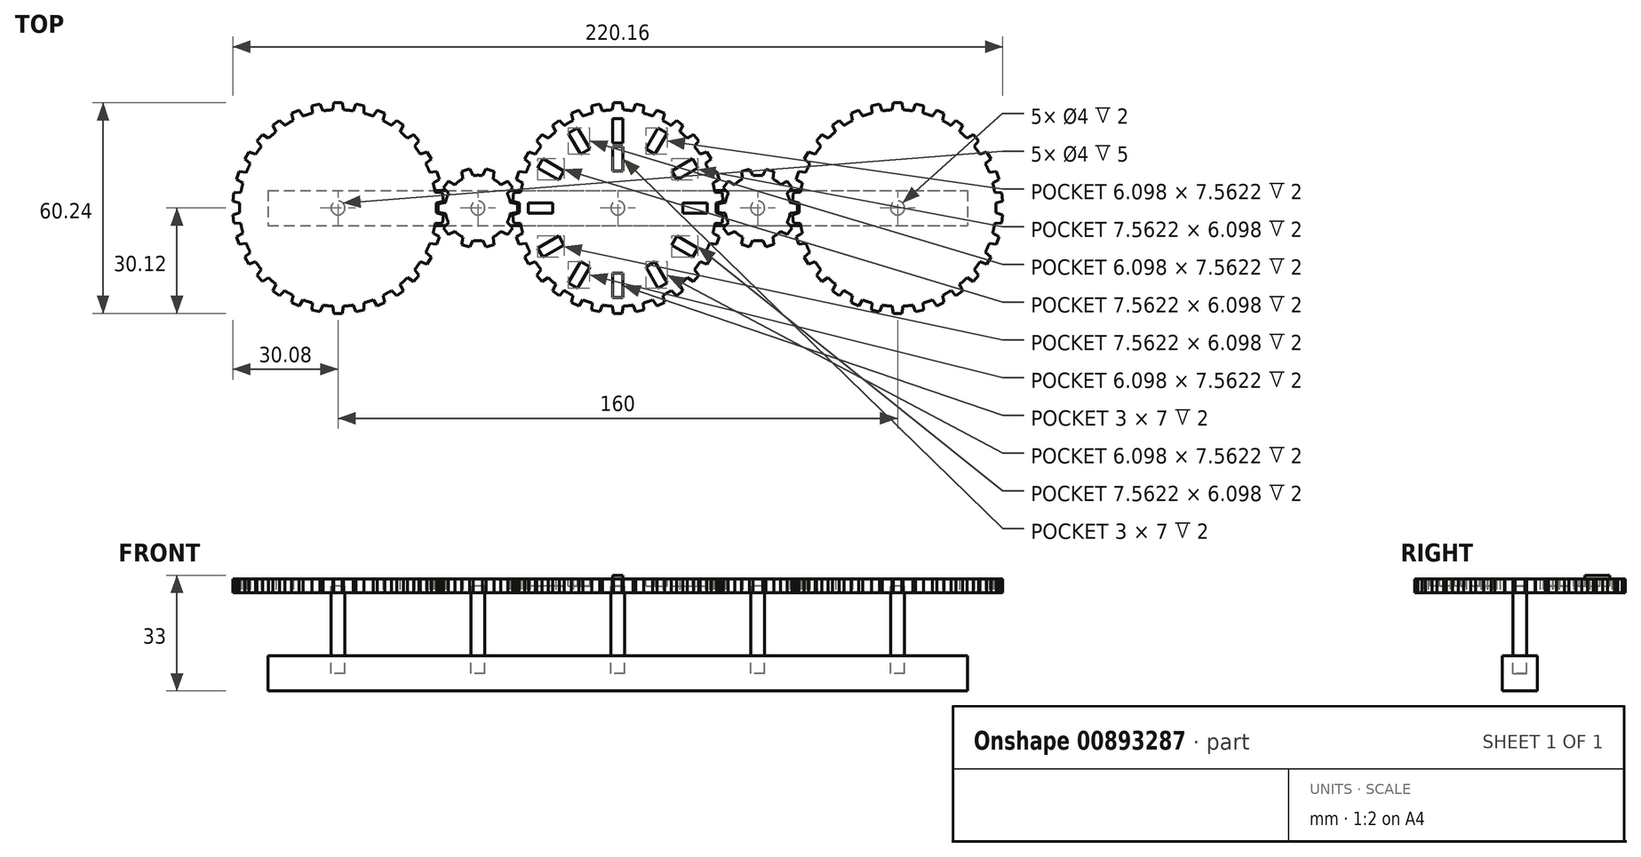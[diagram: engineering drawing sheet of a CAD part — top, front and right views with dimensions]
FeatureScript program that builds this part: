
annotation { "Feature Type Name" : "Feature", "Feature Type Description" : "" }
export const myFeature = defineFeature(function(context is Context, id is Id, definition is map)
    precondition{}
    {
        {
            var Q0;
            Q0=qCreatedBy(makeId("Top.planeOp"),FACE);
            var sketch = newSketch(context, id + "F0", { "sketchPlane" : qUnion([Q0])});
            skCircle(sketch, "E0", {"center": v(0, 0) * mm, "radius": 28.13 * mm});
            skLineSegment(sketch, "E1", {"start": v(-1.54, 28.08) * mm, "end": v(-1.18, 30.13) * mm});
            skLineSegment(sketch, "E2", {"start": v(-1.18, 30.13) * mm, "end": v(0, 30.13) * mm});
            skLineSegment(sketch, "E3.MirrorCS", {"start": v(1.54, 28.08) * mm, "end": v(1.18, 30.13) * mm});
            skLineSegment(sketch, "E4.MirrorCS", {"start": v(1.18, 30.13) * mm, "end": v(0, 30.13) * mm});
            skLineSegment(sketch, "E5.1.0", {"start": v(-7.34, 27.15) * mm, "end": v(-7.42, 29.22) * mm});
            skLineSegment(sketch, "E5.1.1", {"start": v(-7.42, 29.22) * mm, "end": v(-6.26, 29.47) * mm});
            skLineSegment(sketch, "E5.1.2", {"start": v(-5.11, 29.71) * mm, "end": v(-6.26, 29.47) * mm});
            skLineSegment(sketch, "E5.1.3", {"start": v(-4.33, 27.79) * mm, "end": v(-5.11, 29.71) * mm});
            skLineSegment(sketch, "E5.2.0", {"start": v(-12.83, 25.03) * mm, "end": v(-13.33, 27.04) * mm});
            skLineSegment(sketch, "E5.2.1", {"start": v(-13.33, 27.04) * mm, "end": v(-12.25, 27.52) * mm});
            skLineSegment(sketch, "E5.2.2", {"start": v(-11.18, 28) * mm, "end": v(-12.25, 27.52) * mm});
            skLineSegment(sketch, "E5.2.3", {"start": v(-10.02, 26.28) * mm, "end": v(-11.18, 28) * mm});
            skLineSegment(sketch, "E6.1.3.0", {"start": v(-17.75, 21.82) * mm, "end": v(-18.66, 23.68) * mm});
            skLineSegment(sketch, "E6.3.3.0", {"start": v(-18.66, 23.68) * mm, "end": v(-17.7, 24.37) * mm});
            skLineSegment(sketch, "E6.6.3.0", {"start": v(-16.75, 25.06) * mm, "end": v(-17.7, 24.37) * mm});
            skLineSegment(sketch, "E6.9.3.0", {"start": v(-15.26, 23.62) * mm, "end": v(-16.75, 25.06) * mm});
            skLineSegment(sketch, "E6.1.4.0", {"start": v(-21.9, 17.65) * mm, "end": v(-23.18, 19.28) * mm});
            skLineSegment(sketch, "E6.3.4.0", {"start": v(-23.18, 19.28) * mm, "end": v(-22.39, 20.16) * mm});
            skLineSegment(sketch, "E6.6.4.0", {"start": v(-21.6, 21.03) * mm, "end": v(-22.39, 20.16) * mm});
            skLineSegment(sketch, "E6.9.4.0", {"start": v(-19.84, 19.93) * mm, "end": v(-21.6, 21.03) * mm});
            skLineSegment(sketch, "E6.1.5.0", {"start": v(-25.09, 12.7) * mm, "end": v(-26.68, 14.04) * mm});
            skLineSegment(sketch, "E6.3.5.0", {"start": v(-26.68, 14.04) * mm, "end": v(-26.09, 15.06) * mm});
            skLineSegment(sketch, "E6.6.5.0", {"start": v(-25.5, 16.08) * mm, "end": v(-26.09, 15.06) * mm});
            skLineSegment(sketch, "E6.9.5.0", {"start": v(-23.55, 15.37) * mm, "end": v(-25.5, 16.08) * mm});
            skLineSegment(sketch, "E6.1.6.0", {"start": v(-27.18, 7.22) * mm, "end": v(-29.01, 8.19) * mm});
            skLineSegment(sketch, "E6.3.6.0", {"start": v(-29.01, 8.19) * mm, "end": v(-28.65, 9.3) * mm});
            skLineSegment(sketch, "E6.6.6.0", {"start": v(-28.29, 10.43) * mm, "end": v(-28.65, 9.3) * mm});
            skLineSegment(sketch, "E6.9.6.0", {"start": v(-26.23, 10.14) * mm, "end": v(-28.29, 10.43) * mm});
            skLineSegment(sketch, "E6.1.7.0", {"start": v(-28.09, 1.4) * mm, "end": v(-30.08, 1.98) * mm});
            skLineSegment(sketch, "E6.3.7.0", {"start": v(-30.08, 1.98) * mm, "end": v(-29.96, 3.15) * mm});
            skLineSegment(sketch, "E6.6.7.0", {"start": v(-29.84, 4.32) * mm, "end": v(-29.96, 3.15) * mm});
            skLineSegment(sketch, "E6.9.7.0", {"start": v(-27.77, 4.47) * mm, "end": v(-29.84, 4.32) * mm});
            skLineSegment(sketch, "E6.1.8.0", {"start": v(-27.77, -4.47) * mm, "end": v(-29.84, -4.32) * mm});
            skLineSegment(sketch, "E6.3.8.0", {"start": v(-29.84, -4.32) * mm, "end": v(-29.96, -3.15) * mm});
            skLineSegment(sketch, "E6.6.8.0", {"start": v(-30.08, -1.98) * mm, "end": v(-29.96, -3.15) * mm});
            skLineSegment(sketch, "E6.9.8.0", {"start": v(-28.09, -1.4) * mm, "end": v(-30.08, -1.98) * mm});
            skLineSegment(sketch, "E6.1.9.0", {"start": v(-26.23, -10.14) * mm, "end": v(-28.29, -10.43) * mm});
            skLineSegment(sketch, "E6.3.9.0", {"start": v(-28.29, -10.43) * mm, "end": v(-28.65, -9.3) * mm});
            skLineSegment(sketch, "E6.6.9.0", {"start": v(-29.01, -8.19) * mm, "end": v(-28.65, -9.3) * mm});
            skLineSegment(sketch, "E6.9.9.0", {"start": v(-27.18, -7.22) * mm, "end": v(-29.01, -8.19) * mm});
            skLineSegment(sketch, "E7.1.10.0", {"start": v(-23.55, -15.37) * mm, "end": v(-25.5, -16.08) * mm});
            skLineSegment(sketch, "E7.3.10.0", {"start": v(-25.5, -16.08) * mm, "end": v(-26.09, -15.06) * mm});
            skLineSegment(sketch, "E7.6.10.0", {"start": v(-26.68, -14.04) * mm, "end": v(-26.09, -15.06) * mm});
            skLineSegment(sketch, "E7.9.10.0", {"start": v(-25.09, -12.7) * mm, "end": v(-26.68, -14.04) * mm});
            skLineSegment(sketch, "E7.1.11.0", {"start": v(-19.84, -19.93) * mm, "end": v(-21.6, -21.03) * mm});
            skLineSegment(sketch, "E7.3.11.0", {"start": v(-21.6, -21.03) * mm, "end": v(-22.39, -20.16) * mm});
            skLineSegment(sketch, "E7.6.11.0", {"start": v(-23.18, -19.28) * mm, "end": v(-22.39, -20.16) * mm});
            skLineSegment(sketch, "E7.9.11.0", {"start": v(-21.9, -17.65) * mm, "end": v(-23.18, -19.28) * mm});
            skLineSegment(sketch, "E7.1.12.0", {"start": v(-15.26, -23.62) * mm, "end": v(-16.75, -25.06) * mm});
            skLineSegment(sketch, "E7.3.12.0", {"start": v(-16.75, -25.06) * mm, "end": v(-17.7, -24.37) * mm});
            skLineSegment(sketch, "E7.6.12.0", {"start": v(-18.66, -23.68) * mm, "end": v(-17.7, -24.37) * mm});
            skLineSegment(sketch, "E7.9.12.0", {"start": v(-17.75, -21.82) * mm, "end": v(-18.66, -23.68) * mm});
            skLineSegment(sketch, "E7.1.13.0", {"start": v(-10.02, -26.28) * mm, "end": v(-11.18, -28) * mm});
            skLineSegment(sketch, "E7.3.13.0", {"start": v(-11.18, -28) * mm, "end": v(-12.25, -27.52) * mm});
            skLineSegment(sketch, "E7.6.13.0", {"start": v(-13.33, -27.04) * mm, "end": v(-12.25, -27.52) * mm});
            skLineSegment(sketch, "E7.9.13.0", {"start": v(-12.83, -25.03) * mm, "end": v(-13.33, -27.04) * mm});
            skLineSegment(sketch, "E7.1.14.0", {"start": v(-4.33, -27.79) * mm, "end": v(-5.11, -29.71) * mm});
            skLineSegment(sketch, "E7.3.14.0", {"start": v(-5.11, -29.71) * mm, "end": v(-6.26, -29.47) * mm});
            skLineSegment(sketch, "E7.6.14.0", {"start": v(-7.42, -29.22) * mm, "end": v(-6.26, -29.47) * mm});
            skLineSegment(sketch, "E7.9.14.0", {"start": v(-7.34, -27.15) * mm, "end": v(-7.42, -29.22) * mm});
            skLineSegment(sketch, "E7.1.15.0", {"start": v(1.54, -28.08) * mm, "end": v(1.18, -30.13) * mm});
            skLineSegment(sketch, "E7.3.15.0", {"start": v(1.18, -30.13) * mm, "end": v(0, -30.13) * mm});
            skLineSegment(sketch, "E7.6.15.0", {"start": v(-1.18, -30.13) * mm, "end": v(0, -30.13) * mm});
            skLineSegment(sketch, "E7.9.15.0", {"start": v(-1.54, -28.08) * mm, "end": v(-1.18, -30.13) * mm});
            skLineSegment(sketch, "E7.1.16.0", {"start": v(7.34, -27.15) * mm, "end": v(7.42, -29.22) * mm});
            skLineSegment(sketch, "E7.3.16.0", {"start": v(7.42, -29.22) * mm, "end": v(6.26, -29.47) * mm});
            skLineSegment(sketch, "E7.6.16.0", {"start": v(5.11, -29.71) * mm, "end": v(6.26, -29.47) * mm});
            skLineSegment(sketch, "E7.9.16.0", {"start": v(4.33, -27.79) * mm, "end": v(5.11, -29.71) * mm});
            skLineSegment(sketch, "E7.1.17.0", {"start": v(12.83, -25.03) * mm, "end": v(13.33, -27.04) * mm});
            skLineSegment(sketch, "E7.3.17.0", {"start": v(13.33, -27.04) * mm, "end": v(12.25, -27.52) * mm});
            skLineSegment(sketch, "E7.6.17.0", {"start": v(11.18, -28) * mm, "end": v(12.25, -27.52) * mm});
            skLineSegment(sketch, "E7.9.17.0", {"start": v(10.02, -26.28) * mm, "end": v(11.18, -28) * mm});
            skLineSegment(sketch, "E7.1.18.0", {"start": v(17.75, -21.82) * mm, "end": v(18.66, -23.68) * mm});
            skLineSegment(sketch, "E7.3.18.0", {"start": v(18.66, -23.68) * mm, "end": v(17.7, -24.37) * mm});
            skLineSegment(sketch, "E7.6.18.0", {"start": v(16.75, -25.06) * mm, "end": v(17.7, -24.37) * mm});
            skLineSegment(sketch, "E7.9.18.0", {"start": v(15.26, -23.62) * mm, "end": v(16.75, -25.06) * mm});
            skLineSegment(sketch, "E7.1.19.0", {"start": v(21.9, -17.65) * mm, "end": v(23.18, -19.28) * mm});
            skLineSegment(sketch, "E7.3.19.0", {"start": v(23.18, -19.28) * mm, "end": v(22.39, -20.16) * mm});
            skLineSegment(sketch, "E7.6.19.0", {"start": v(21.6, -21.03) * mm, "end": v(22.39, -20.16) * mm});
            skLineSegment(sketch, "E7.9.19.0", {"start": v(19.84, -19.93) * mm, "end": v(21.6, -21.03) * mm});
            skLineSegment(sketch, "E7.1.20.0", {"start": v(25.09, -12.7) * mm, "end": v(26.68, -14.04) * mm});
            skLineSegment(sketch, "E7.3.20.0", {"start": v(26.68, -14.04) * mm, "end": v(26.09, -15.06) * mm});
            skLineSegment(sketch, "E7.6.20.0", {"start": v(25.5, -16.08) * mm, "end": v(26.09, -15.06) * mm});
            skLineSegment(sketch, "E7.9.20.0", {"start": v(23.55, -15.37) * mm, "end": v(25.5, -16.08) * mm});
            skLineSegment(sketch, "E7.1.21.0", {"start": v(27.18, -7.22) * mm, "end": v(29.01, -8.19) * mm});
            skLineSegment(sketch, "E7.3.21.0", {"start": v(29.01, -8.19) * mm, "end": v(28.65, -9.3) * mm});
            skLineSegment(sketch, "E7.6.21.0", {"start": v(28.29, -10.43) * mm, "end": v(28.65, -9.3) * mm});
            skLineSegment(sketch, "E7.9.21.0", {"start": v(26.23, -10.14) * mm, "end": v(28.29, -10.43) * mm});
            skLineSegment(sketch, "E7.1.22.0", {"start": v(28.09, -1.4) * mm, "end": v(30.08, -1.98) * mm});
            skLineSegment(sketch, "E7.3.22.0", {"start": v(30.08, -1.98) * mm, "end": v(29.96, -3.15) * mm});
            skLineSegment(sketch, "E7.6.22.0", {"start": v(29.84, -4.32) * mm, "end": v(29.96, -3.15) * mm});
            skLineSegment(sketch, "E7.9.22.0", {"start": v(27.77, -4.47) * mm, "end": v(29.84, -4.32) * mm});
            skLineSegment(sketch, "E7.1.23.0", {"start": v(27.77, 4.47) * mm, "end": v(29.84, 4.32) * mm});
            skLineSegment(sketch, "E7.3.23.0", {"start": v(29.84, 4.32) * mm, "end": v(29.96, 3.15) * mm});
            skLineSegment(sketch, "E7.6.23.0", {"start": v(30.08, 1.98) * mm, "end": v(29.96, 3.15) * mm});
            skLineSegment(sketch, "E7.9.23.0", {"start": v(28.09, 1.4) * mm, "end": v(30.08, 1.98) * mm});
            skLineSegment(sketch, "E7.1.24.0", {"start": v(26.23, 10.14) * mm, "end": v(28.29, 10.43) * mm});
            skLineSegment(sketch, "E7.3.24.0", {"start": v(28.29, 10.43) * mm, "end": v(28.65, 9.3) * mm});
            skLineSegment(sketch, "E7.6.24.0", {"start": v(29.01, 8.19) * mm, "end": v(28.65, 9.3) * mm});
            skLineSegment(sketch, "E7.9.24.0", {"start": v(27.18, 7.22) * mm, "end": v(29.01, 8.19) * mm});
            skLineSegment(sketch, "E7.1.25.0", {"start": v(23.55, 15.37) * mm, "end": v(25.5, 16.08) * mm});
            skLineSegment(sketch, "E7.3.25.0", {"start": v(25.5, 16.08) * mm, "end": v(26.09, 15.06) * mm});
            skLineSegment(sketch, "E7.6.25.0", {"start": v(26.68, 14.04) * mm, "end": v(26.09, 15.06) * mm});
            skLineSegment(sketch, "E7.9.25.0", {"start": v(25.09, 12.7) * mm, "end": v(26.68, 14.04) * mm});
            skLineSegment(sketch, "E7.1.26.0", {"start": v(19.84, 19.93) * mm, "end": v(21.6, 21.03) * mm});
            skLineSegment(sketch, "E7.3.26.0", {"start": v(21.6, 21.03) * mm, "end": v(22.39, 20.16) * mm});
            skLineSegment(sketch, "E7.6.26.0", {"start": v(23.18, 19.28) * mm, "end": v(22.39, 20.16) * mm});
            skLineSegment(sketch, "E7.9.26.0", {"start": v(21.9, 17.65) * mm, "end": v(23.18, 19.28) * mm});
            skLineSegment(sketch, "E7.1.27.0", {"start": v(15.26, 23.62) * mm, "end": v(16.75, 25.06) * mm});
            skLineSegment(sketch, "E7.3.27.0", {"start": v(16.75, 25.06) * mm, "end": v(17.7, 24.37) * mm});
            skLineSegment(sketch, "E7.6.27.0", {"start": v(18.66, 23.68) * mm, "end": v(17.7, 24.37) * mm});
            skLineSegment(sketch, "E7.9.27.0", {"start": v(17.75, 21.82) * mm, "end": v(18.66, 23.68) * mm});
            skLineSegment(sketch, "E7.1.28.0", {"start": v(10.02, 26.28) * mm, "end": v(11.18, 28) * mm});
            skLineSegment(sketch, "E7.3.28.0", {"start": v(11.18, 28) * mm, "end": v(12.25, 27.52) * mm});
            skLineSegment(sketch, "E7.6.28.0", {"start": v(13.33, 27.04) * mm, "end": v(12.25, 27.52) * mm});
            skLineSegment(sketch, "E7.9.28.0", {"start": v(12.83, 25.03) * mm, "end": v(13.33, 27.04) * mm});
            skLineSegment(sketch, "E7.1.29.0", {"start": v(4.33, 27.79) * mm, "end": v(5.11, 29.71) * mm});
            skLineSegment(sketch, "E7.3.29.0", {"start": v(5.11, 29.71) * mm, "end": v(6.26, 29.47) * mm});
            skLineSegment(sketch, "E7.6.29.0", {"start": v(7.42, 29.22) * mm, "end": v(6.26, 29.47) * mm});
            skLineSegment(sketch, "E7.9.29.0", {"start": v(7.34, 27.15) * mm, "end": v(7.42, 29.22) * mm});
            skSolve(sketch);
        }
        {
            var Q0;
            Q0 = qSketchRegion(id + "F0", true);
            extrude(context, id + "F1", {"entities" : qUnion([Q0]), "endBound" : BoundingType.SYMMETRIC, "depth" : 4 * mm, "offsetDistance" : 25 * mm});
        }
        {
            var Q0;
            Q0=qCreatedBy(makeId("Top.planeOp"),FACE);
            var sketch = newSketch(context, id + "F2", { "sketchPlane" : qUnion([Q0])});
            skCircle(sketch, "E8", {"center": v(40, 0) * mm, "radius": 9.38 * mm});
            skLineSegment(sketch, "E9", {"start": v(30.75, 1.54) * mm, "end": v(28.69, 1.18) * mm});
            skLineSegment(sketch, "E10", {"start": v(28.69, 1.18) * mm, "end": v(28.69, 0) * mm});
            skLineSegment(sketch, "E11.MirrorCS", {"start": v(28.69, -1.18) * mm, "end": v(28.69, 0) * mm});
            skLineSegment(sketch, "E12.MirrorCS", {"start": v(30.75, -1.54) * mm, "end": v(28.69, -1.18) * mm});
            skLineSegment(sketch, "E13.1.0", {"start": v(31.61, -4.19) * mm, "end": v(30.15, -5.7) * mm});
            skLineSegment(sketch, "E13.1.1", {"start": v(30.15, -5.7) * mm, "end": v(30.85, -6.65) * mm});
            skLineSegment(sketch, "E13.1.2", {"start": v(31.54, -7.6) * mm, "end": v(30.85, -6.65) * mm});
            skLineSegment(sketch, "E13.1.3", {"start": v(33.43, -6.68) * mm, "end": v(31.54, -7.6) * mm});
            skLineSegment(sketch, "E13.2.0", {"start": v(35.68, -8.32) * mm, "end": v(35.38, -10.4) * mm});
            skLineSegment(sketch, "E13.2.1", {"start": v(35.38, -10.4) * mm, "end": v(36.5, -10.76) * mm});
            skLineSegment(sketch, "E13.2.2", {"start": v(37.62, -11.12) * mm, "end": v(36.5, -10.76) * mm});
            skLineSegment(sketch, "E13.2.3", {"start": v(38.6, -9.27) * mm, "end": v(37.62, -11.12) * mm});
            skLineSegment(sketch, "E14.2.3.0", {"start": v(41.4, -9.27) * mm, "end": v(42.38, -11.12) * mm});
            skLineSegment(sketch, "E14.3.3.0", {"start": v(42.38, -11.12) * mm, "end": v(43.5, -10.76) * mm});
            skLineSegment(sketch, "E14.6.3.0", {"start": v(44.62, -10.4) * mm, "end": v(43.5, -10.76) * mm});
            skLineSegment(sketch, "E14.9.3.0", {"start": v(44.32, -8.32) * mm, "end": v(44.62, -10.4) * mm});
            skLineSegment(sketch, "E14.2.4.0", {"start": v(46.57, -6.68) * mm, "end": v(48.46, -7.6) * mm});
            skLineSegment(sketch, "E14.3.4.0", {"start": v(48.46, -7.6) * mm, "end": v(49.15, -6.65) * mm});
            skLineSegment(sketch, "E14.6.4.0", {"start": v(49.85, -5.7) * mm, "end": v(49.15, -6.65) * mm});
            skLineSegment(sketch, "E14.9.4.0", {"start": v(48.39, -4.19) * mm, "end": v(49.85, -5.7) * mm});
            skLineSegment(sketch, "E14.2.5.0", {"start": v(49.25, -1.54) * mm, "end": v(51.31, -1.18) * mm});
            skLineSegment(sketch, "E14.3.5.0", {"start": v(51.31, -1.18) * mm, "end": v(51.31, 0) * mm});
            skLineSegment(sketch, "E14.6.5.0", {"start": v(51.31, 1.18) * mm, "end": v(51.31, 0) * mm});
            skLineSegment(sketch, "E14.9.5.0", {"start": v(49.25, 1.54) * mm, "end": v(51.31, 1.18) * mm});
            skLineSegment(sketch, "E14.2.6.0", {"start": v(48.39, 4.19) * mm, "end": v(49.85, 5.7) * mm});
            skLineSegment(sketch, "E14.3.6.0", {"start": v(49.85, 5.7) * mm, "end": v(49.15, 6.65) * mm});
            skLineSegment(sketch, "E14.6.6.0", {"start": v(48.46, 7.6) * mm, "end": v(49.15, 6.65) * mm});
            skLineSegment(sketch, "E14.9.6.0", {"start": v(46.57, 6.68) * mm, "end": v(48.46, 7.6) * mm});
            skLineSegment(sketch, "E14.2.7.0", {"start": v(44.32, 8.32) * mm, "end": v(44.62, 10.4) * mm});
            skLineSegment(sketch, "E14.3.7.0", {"start": v(44.62, 10.4) * mm, "end": v(43.5, 10.76) * mm});
            skLineSegment(sketch, "E14.6.7.0", {"start": v(42.38, 11.12) * mm, "end": v(43.5, 10.76) * mm});
            skLineSegment(sketch, "E14.9.7.0", {"start": v(41.4, 9.27) * mm, "end": v(42.38, 11.12) * mm});
            skLineSegment(sketch, "E14.2.8.0", {"start": v(38.6, 9.27) * mm, "end": v(37.62, 11.12) * mm});
            skLineSegment(sketch, "E14.3.8.0", {"start": v(37.62, 11.12) * mm, "end": v(36.5, 10.76) * mm});
            skLineSegment(sketch, "E14.6.8.0", {"start": v(35.38, 10.4) * mm, "end": v(36.5, 10.76) * mm});
            skLineSegment(sketch, "E14.9.8.0", {"start": v(35.68, 8.32) * mm, "end": v(35.38, 10.4) * mm});
            skLineSegment(sketch, "E14.2.9.0", {"start": v(33.43, 6.68) * mm, "end": v(31.54, 7.6) * mm});
            skLineSegment(sketch, "E14.3.9.0", {"start": v(31.54, 7.6) * mm, "end": v(30.85, 6.65) * mm});
            skLineSegment(sketch, "E14.6.9.0", {"start": v(30.15, 5.7) * mm, "end": v(30.85, 6.65) * mm});
            skLineSegment(sketch, "E14.9.9.0", {"start": v(31.61, 4.19) * mm, "end": v(30.15, 5.7) * mm});
            skCircle(sketch, "E15.MirrorC", {"center": v(-40, 0) * mm, "radius": 9.38 * mm});
            skLineSegment(sketch, "E16", {"start": v(-30.75, 1.55) * mm, "end": v(-28.62, 1.18) * mm});
            skLineSegment(sketch, "E17", {"start": v(-28.62, 1.18) * mm, "end": v(-28.62, 0) * mm});
            skLineSegment(sketch, "E18.MirrorCS", {"start": v(-30.75, -1.55) * mm, "end": v(-28.62, -1.18) * mm});
            skLineSegment(sketch, "E19.MirrorCS", {"start": v(-28.62, -1.18) * mm, "end": v(-28.62, 0) * mm});
            skLineSegment(sketch, "E20.1.0", {"start": v(-33.43, 6.7) * mm, "end": v(-31.49, 7.64) * mm});
            skLineSegment(sketch, "E20.1.1", {"start": v(-31.49, 7.64) * mm, "end": v(-30.8, 6.69) * mm});
            skLineSegment(sketch, "E20.1.2", {"start": v(-30.1, 5.73) * mm, "end": v(-30.8, 6.69) * mm});
            skLineSegment(sketch, "E20.1.3", {"start": v(-31.6, 4.18) * mm, "end": v(-30.1, 5.73) * mm});
            skLineSegment(sketch, "E20.2.0", {"start": v(-38.62, 9.27) * mm, "end": v(-37.6, 11.18) * mm});
            skLineSegment(sketch, "E20.2.1", {"start": v(-37.6, 11.18) * mm, "end": v(-36.48, 10.82) * mm});
            skLineSegment(sketch, "E20.2.2", {"start": v(-35.36, 10.45) * mm, "end": v(-36.48, 10.82) * mm});
            skLineSegment(sketch, "E20.2.3", {"start": v(-35.67, 8.31) * mm, "end": v(-35.36, 10.45) * mm});
            skLineSegment(sketch, "E21.1.3.0", {"start": v(-44.33, 8.31) * mm, "end": v(-44.64, 10.45) * mm});
            skLineSegment(sketch, "E21.3.3.0", {"start": v(-44.64, 10.45) * mm, "end": v(-43.52, 10.82) * mm});
            skLineSegment(sketch, "E21.6.3.0", {"start": v(-42.4, 11.18) * mm, "end": v(-43.52, 10.82) * mm});
            skLineSegment(sketch, "E21.9.3.0", {"start": v(-41.38, 9.27) * mm, "end": v(-42.4, 11.18) * mm});
            skLineSegment(sketch, "E21.1.4.0", {"start": v(-48.4, 4.18) * mm, "end": v(-49.9, 5.73) * mm});
            skLineSegment(sketch, "E21.3.4.0", {"start": v(-49.9, 5.73) * mm, "end": v(-49.2, 6.69) * mm});
            skLineSegment(sketch, "E21.6.4.0", {"start": v(-48.51, 7.64) * mm, "end": v(-49.2, 6.69) * mm});
            skLineSegment(sketch, "E21.9.4.0", {"start": v(-46.57, 6.7) * mm, "end": v(-48.51, 7.64) * mm});
            skLineSegment(sketch, "E21.1.5.0", {"start": v(-49.25, -1.55) * mm, "end": v(-51.38, -1.18) * mm});
            skLineSegment(sketch, "E21.3.5.0", {"start": v(-51.38, -1.18) * mm, "end": v(-51.38, 0) * mm});
            skLineSegment(sketch, "E21.6.5.0", {"start": v(-51.38, 1.18) * mm, "end": v(-51.38, 0) * mm});
            skLineSegment(sketch, "E21.9.5.0", {"start": v(-49.25, 1.55) * mm, "end": v(-51.38, 1.18) * mm});
            skLineSegment(sketch, "E21.1.6.0", {"start": v(-46.57, -6.7) * mm, "end": v(-48.51, -7.64) * mm});
            skLineSegment(sketch, "E21.3.6.0", {"start": v(-48.51, -7.64) * mm, "end": v(-49.2, -6.69) * mm});
            skLineSegment(sketch, "E21.6.6.0", {"start": v(-49.9, -5.73) * mm, "end": v(-49.2, -6.69) * mm});
            skLineSegment(sketch, "E21.9.6.0", {"start": v(-48.4, -4.18) * mm, "end": v(-49.9, -5.73) * mm});
            skLineSegment(sketch, "E21.1.7.0", {"start": v(-41.38, -9.27) * mm, "end": v(-42.4, -11.18) * mm});
            skLineSegment(sketch, "E21.3.7.0", {"start": v(-42.4, -11.18) * mm, "end": v(-43.52, -10.82) * mm});
            skLineSegment(sketch, "E21.6.7.0", {"start": v(-44.64, -10.45) * mm, "end": v(-43.52, -10.82) * mm});
            skLineSegment(sketch, "E21.9.7.0", {"start": v(-44.33, -8.31) * mm, "end": v(-44.64, -10.45) * mm});
            skLineSegment(sketch, "E21.1.8.0", {"start": v(-35.67, -8.31) * mm, "end": v(-35.36, -10.45) * mm});
            skLineSegment(sketch, "E21.3.8.0", {"start": v(-35.36, -10.45) * mm, "end": v(-36.48, -10.82) * mm});
            skLineSegment(sketch, "E21.6.8.0", {"start": v(-37.6, -11.18) * mm, "end": v(-36.48, -10.82) * mm});
            skLineSegment(sketch, "E21.9.8.0", {"start": v(-38.62, -9.27) * mm, "end": v(-37.6, -11.18) * mm});
            skLineSegment(sketch, "E21.1.9.0", {"start": v(-31.6, -4.18) * mm, "end": v(-30.1, -5.73) * mm});
            skLineSegment(sketch, "E21.3.9.0", {"start": v(-30.1, -5.73) * mm, "end": v(-30.8, -6.69) * mm});
            skLineSegment(sketch, "E21.6.9.0", {"start": v(-31.49, -7.64) * mm, "end": v(-30.8, -6.69) * mm});
            skLineSegment(sketch, "E21.9.9.0", {"start": v(-33.43, -6.7) * mm, "end": v(-31.49, -7.64) * mm});
            skCircle(sketch, "E22", {"center": v(-80, 0) * mm, "radius": 28.13 * mm});
            skLineSegment(sketch, "E23", {"start": v(-80, 30.12) * mm, "end": v(-78.82, 30.12) * mm});
            skLineSegment(sketch, "E24", {"start": v(-78.82, 30.12) * mm, "end": v(-78.46, 28.08) * mm});
            skLineSegment(sketch, "E25", {"start": v(-80, 30.12) * mm, "end": v(-81.18, 30.12) * mm});
            skLineSegment(sketch, "E26", {"start": v(-81.18, 30.13) * mm, "end": v(-81.54, 28.08) * mm});
            skCircle(sketch, "E27.MirrorC", {"center": v(80, 0) * mm, "radius": 28.13 * mm});
            skLineSegment(sketch, "E28.MirrorCS", {"start": v(81.18, 30.13) * mm, "end": v(81.54, 28.08) * mm});
            skLineSegment(sketch, "E29.MirrorCS", {"start": v(80, 30.12) * mm, "end": v(81.18, 30.12) * mm});
            skLineSegment(sketch, "E30.MirrorCS", {"start": v(80, 30.12) * mm, "end": v(78.82, 30.12) * mm});
            skLineSegment(sketch, "E31.MirrorCS", {"start": v(78.82, 30.12) * mm, "end": v(78.46, 28.08) * mm});
            skLineSegment(sketch, "E32.1.0", {"start": v(-85.11, 29.71) * mm, "end": v(-84.33, 27.79) * mm});
            skLineSegment(sketch, "E32.1.1", {"start": v(-86.26, 29.47) * mm, "end": v(-85.11, 29.71) * mm});
            skLineSegment(sketch, "E32.1.2", {"start": v(-86.26, 29.47) * mm, "end": v(-87.42, 29.22) * mm});
            skLineSegment(sketch, "E32.1.3", {"start": v(-87.42, 29.22) * mm, "end": v(-87.34, 27.15) * mm});
            skLineSegment(sketch, "E32.2.0", {"start": v(-91.18, 28) * mm, "end": v(-90.02, 26.28) * mm});
            skLineSegment(sketch, "E32.2.1", {"start": v(-92.25, 27.52) * mm, "end": v(-91.18, 28) * mm});
            skLineSegment(sketch, "E32.2.2", {"start": v(-92.25, 27.52) * mm, "end": v(-93.33, 27.04) * mm});
            skLineSegment(sketch, "E32.2.3", {"start": v(-93.33, 27.04) * mm, "end": v(-92.83, 25.03) * mm});
            skLineSegment(sketch, "E33.2.3.0", {"start": v(-96.75, 25.06) * mm, "end": v(-95.26, 23.62) * mm});
            skLineSegment(sketch, "E33.3.3.0", {"start": v(-97.7, 24.37) * mm, "end": v(-96.75, 25.06) * mm});
            skLineSegment(sketch, "E33.6.3.0", {"start": v(-97.7, 24.37) * mm, "end": v(-98.66, 23.68) * mm});
            skLineSegment(sketch, "E33.9.3.0", {"start": v(-98.66, 23.68) * mm, "end": v(-97.75, 21.82) * mm});
            skLineSegment(sketch, "E33.2.4.0", {"start": v(-101.6, 21.03) * mm, "end": v(-99.84, 19.93) * mm});
            skLineSegment(sketch, "E33.3.4.0", {"start": v(-102.39, 20.16) * mm, "end": v(-101.6, 21.03) * mm});
            skLineSegment(sketch, "E33.6.4.0", {"start": v(-102.39, 20.16) * mm, "end": v(-103.18, 19.28) * mm});
            skLineSegment(sketch, "E33.9.4.0", {"start": v(-103.18, 19.28) * mm, "end": v(-101.9, 17.65) * mm});
            skLineSegment(sketch, "E33.2.5.0", {"start": v(-105.5, 16.08) * mm, "end": v(-103.55, 15.37) * mm});
            skLineSegment(sketch, "E33.3.5.0", {"start": v(-106.09, 15.06) * mm, "end": v(-105.5, 16.08) * mm});
            skLineSegment(sketch, "E33.6.5.0", {"start": v(-106.09, 15.06) * mm, "end": v(-106.68, 14.04) * mm});
            skLineSegment(sketch, "E33.9.5.0", {"start": v(-106.68, 14.04) * mm, "end": v(-105.09, 12.7) * mm});
            skLineSegment(sketch, "E33.2.6.0", {"start": v(-108.29, 10.43) * mm, "end": v(-106.23, 10.14) * mm});
            skLineSegment(sketch, "E33.3.6.0", {"start": v(-108.65, 9.3) * mm, "end": v(-108.29, 10.43) * mm});
            skLineSegment(sketch, "E33.6.6.0", {"start": v(-108.65, 9.3) * mm, "end": v(-109.01, 8.19) * mm});
            skLineSegment(sketch, "E33.9.6.0", {"start": v(-109.01, 8.19) * mm, "end": v(-107.18, 7.22) * mm});
            skLineSegment(sketch, "E33.2.7.0", {"start": v(-109.84, 4.32) * mm, "end": v(-107.77, 4.47) * mm});
            skLineSegment(sketch, "E33.3.7.0", {"start": v(-109.96, 3.15) * mm, "end": v(-109.84, 4.32) * mm});
            skLineSegment(sketch, "E33.6.7.0", {"start": v(-109.96, 3.15) * mm, "end": v(-110.08, 1.98) * mm});
            skLineSegment(sketch, "E33.9.7.0", {"start": v(-110.08, 1.98) * mm, "end": v(-108.09, 1.4) * mm});
            skLineSegment(sketch, "E33.2.8.0", {"start": v(-110.08, -1.98) * mm, "end": v(-108.09, -1.4) * mm});
            skLineSegment(sketch, "E33.3.8.0", {"start": v(-109.96, -3.15) * mm, "end": v(-110.08, -1.98) * mm});
            skLineSegment(sketch, "E33.6.8.0", {"start": v(-109.96, -3.15) * mm, "end": v(-109.84, -4.32) * mm});
            skLineSegment(sketch, "E33.9.8.0", {"start": v(-109.84, -4.32) * mm, "end": v(-107.77, -4.47) * mm});
            skLineSegment(sketch, "E33.2.9.0", {"start": v(-109.01, -8.19) * mm, "end": v(-107.18, -7.22) * mm});
            skLineSegment(sketch, "E33.3.9.0", {"start": v(-108.65, -9.3) * mm, "end": v(-109.01, -8.19) * mm});
            skLineSegment(sketch, "E33.6.9.0", {"start": v(-108.65, -9.3) * mm, "end": v(-108.29, -10.43) * mm});
            skLineSegment(sketch, "E33.9.9.0", {"start": v(-108.29, -10.43) * mm, "end": v(-106.23, -10.14) * mm});
            skLineSegment(sketch, "E33.2.10.0", {"start": v(-106.68, -14.04) * mm, "end": v(-105.09, -12.7) * mm});
            skLineSegment(sketch, "E33.3.10.0", {"start": v(-106.09, -15.06) * mm, "end": v(-106.68, -14.04) * mm});
            skLineSegment(sketch, "E33.6.10.0", {"start": v(-106.09, -15.06) * mm, "end": v(-105.5, -16.08) * mm});
            skLineSegment(sketch, "E33.9.10.0", {"start": v(-105.5, -16.08) * mm, "end": v(-103.55, -15.37) * mm});
            skLineSegment(sketch, "E33.2.11.0", {"start": v(-103.18, -19.28) * mm, "end": v(-101.9, -17.65) * mm});
            skLineSegment(sketch, "E33.3.11.0", {"start": v(-102.39, -20.16) * mm, "end": v(-103.18, -19.28) * mm});
            skLineSegment(sketch, "E33.6.11.0", {"start": v(-102.39, -20.16) * mm, "end": v(-101.6, -21.03) * mm});
            skLineSegment(sketch, "E33.9.11.0", {"start": v(-101.6, -21.03) * mm, "end": v(-99.84, -19.93) * mm});
            skLineSegment(sketch, "E33.2.12.0", {"start": v(-98.66, -23.68) * mm, "end": v(-97.75, -21.82) * mm});
            skLineSegment(sketch, "E33.3.12.0", {"start": v(-97.7, -24.37) * mm, "end": v(-98.66, -23.68) * mm});
            skLineSegment(sketch, "E33.6.12.0", {"start": v(-97.7, -24.37) * mm, "end": v(-96.75, -25.06) * mm});
            skLineSegment(sketch, "E33.9.12.0", {"start": v(-96.75, -25.06) * mm, "end": v(-95.26, -23.62) * mm});
            skLineSegment(sketch, "E33.2.13.0", {"start": v(-93.33, -27.04) * mm, "end": v(-92.83, -25.03) * mm});
            skLineSegment(sketch, "E33.3.13.0", {"start": v(-92.25, -27.52) * mm, "end": v(-93.33, -27.04) * mm});
            skLineSegment(sketch, "E33.6.13.0", {"start": v(-92.25, -27.52) * mm, "end": v(-91.18, -28) * mm});
            skLineSegment(sketch, "E33.9.13.0", {"start": v(-91.18, -28) * mm, "end": v(-90.02, -26.28) * mm});
            skLineSegment(sketch, "E33.2.14.0", {"start": v(-87.42, -29.22) * mm, "end": v(-87.34, -27.15) * mm});
            skLineSegment(sketch, "E33.3.14.0", {"start": v(-86.26, -29.47) * mm, "end": v(-87.42, -29.22) * mm});
            skLineSegment(sketch, "E33.6.14.0", {"start": v(-86.26, -29.47) * mm, "end": v(-85.11, -29.71) * mm});
            skLineSegment(sketch, "E33.9.14.0", {"start": v(-85.11, -29.71) * mm, "end": v(-84.33, -27.79) * mm});
            skLineSegment(sketch, "E33.2.15.0", {"start": v(-81.18, -30.13) * mm, "end": v(-81.54, -28.08) * mm});
            skLineSegment(sketch, "E33.3.15.0", {"start": v(-80, -30.13) * mm, "end": v(-81.18, -30.13) * mm});
            skLineSegment(sketch, "E33.6.15.0", {"start": v(-80, -30.13) * mm, "end": v(-78.82, -30.13) * mm});
            skLineSegment(sketch, "E33.9.15.0", {"start": v(-78.82, -30.13) * mm, "end": v(-78.46, -28.08) * mm});
            skLineSegment(sketch, "E33.2.16.0", {"start": v(-74.89, -29.71) * mm, "end": v(-75.67, -27.79) * mm});
            skLineSegment(sketch, "E33.3.16.0", {"start": v(-73.74, -29.47) * mm, "end": v(-74.89, -29.71) * mm});
            skLineSegment(sketch, "E33.6.16.0", {"start": v(-73.74, -29.47) * mm, "end": v(-72.58, -29.22) * mm});
            skLineSegment(sketch, "E33.9.16.0", {"start": v(-72.58, -29.22) * mm, "end": v(-72.66, -27.15) * mm});
            skLineSegment(sketch, "E33.2.17.0", {"start": v(-68.82, -28) * mm, "end": v(-69.98, -26.28) * mm});
            skLineSegment(sketch, "E33.3.17.0", {"start": v(-67.75, -27.52) * mm, "end": v(-68.82, -28) * mm});
            skLineSegment(sketch, "E33.6.17.0", {"start": v(-67.75, -27.52) * mm, "end": v(-66.67, -27.04) * mm});
            skLineSegment(sketch, "E33.9.17.0", {"start": v(-66.67, -27.04) * mm, "end": v(-67.17, -25.03) * mm});
            skLineSegment(sketch, "E33.2.18.0", {"start": v(-63.25, -25.06) * mm, "end": v(-64.74, -23.62) * mm});
            skLineSegment(sketch, "E33.3.18.0", {"start": v(-62.3, -24.37) * mm, "end": v(-63.25, -25.06) * mm});
            skLineSegment(sketch, "E33.6.18.0", {"start": v(-62.3, -24.37) * mm, "end": v(-61.34, -23.68) * mm});
            skLineSegment(sketch, "E33.9.18.0", {"start": v(-61.34, -23.68) * mm, "end": v(-62.25, -21.82) * mm});
            skLineSegment(sketch, "E33.2.19.0", {"start": v(-58.4, -21.03) * mm, "end": v(-60.16, -19.93) * mm});
            skLineSegment(sketch, "E33.3.19.0", {"start": v(-57.61, -20.16) * mm, "end": v(-58.4, -21.03) * mm});
            skLineSegment(sketch, "E33.6.19.0", {"start": v(-57.61, -20.16) * mm, "end": v(-56.82, -19.28) * mm});
            skLineSegment(sketch, "E33.9.19.0", {"start": v(-56.82, -19.28) * mm, "end": v(-58.1, -17.65) * mm});
            skLineSegment(sketch, "E33.2.20.0", {"start": v(-54.5, -16.08) * mm, "end": v(-56.45, -15.37) * mm});
            skLineSegment(sketch, "E33.3.20.0", {"start": v(-53.91, -15.06) * mm, "end": v(-54.5, -16.08) * mm});
            skLineSegment(sketch, "E33.6.20.0", {"start": v(-53.91, -15.06) * mm, "end": v(-53.32, -14.04) * mm});
            skLineSegment(sketch, "E33.9.20.0", {"start": v(-53.32, -14.04) * mm, "end": v(-54.91, -12.7) * mm});
            skLineSegment(sketch, "E33.2.21.0", {"start": v(-51.71, -10.43) * mm, "end": v(-53.77, -10.14) * mm});
            skLineSegment(sketch, "E33.3.21.0", {"start": v(-51.35, -9.3) * mm, "end": v(-51.71, -10.43) * mm});
            skLineSegment(sketch, "E33.6.21.0", {"start": v(-51.35, -9.3) * mm, "end": v(-50.99, -8.19) * mm});
            skLineSegment(sketch, "E33.9.21.0", {"start": v(-50.99, -8.19) * mm, "end": v(-52.82, -7.22) * mm});
            skLineSegment(sketch, "E33.2.22.0", {"start": v(-50.16, -4.32) * mm, "end": v(-52.23, -4.47) * mm});
            skLineSegment(sketch, "E33.3.22.0", {"start": v(-50.04, -3.15) * mm, "end": v(-50.16, -4.32) * mm});
            skLineSegment(sketch, "E33.6.22.0", {"start": v(-50.04, -3.15) * mm, "end": v(-49.92, -1.98) * mm});
            skLineSegment(sketch, "E33.9.22.0", {"start": v(-49.92, -1.98) * mm, "end": v(-51.91, -1.4) * mm});
            skLineSegment(sketch, "E33.2.23.0", {"start": v(-49.92, 1.98) * mm, "end": v(-51.91, 1.4) * mm});
            skLineSegment(sketch, "E33.3.23.0", {"start": v(-50.04, 3.15) * mm, "end": v(-49.92, 1.98) * mm});
            skLineSegment(sketch, "E33.6.23.0", {"start": v(-50.04, 3.15) * mm, "end": v(-50.16, 4.32) * mm});
            skLineSegment(sketch, "E33.9.23.0", {"start": v(-50.16, 4.32) * mm, "end": v(-52.23, 4.47) * mm});
            skLineSegment(sketch, "E33.2.24.0", {"start": v(-50.99, 8.19) * mm, "end": v(-52.82, 7.22) * mm});
            skLineSegment(sketch, "E33.3.24.0", {"start": v(-51.35, 9.3) * mm, "end": v(-50.99, 8.19) * mm});
            skLineSegment(sketch, "E33.6.24.0", {"start": v(-51.35, 9.3) * mm, "end": v(-51.71, 10.43) * mm});
            skLineSegment(sketch, "E33.9.24.0", {"start": v(-51.71, 10.43) * mm, "end": v(-53.77, 10.14) * mm});
            skLineSegment(sketch, "E33.2.25.0", {"start": v(-53.32, 14.04) * mm, "end": v(-54.91, 12.7) * mm});
            skLineSegment(sketch, "E33.3.25.0", {"start": v(-53.91, 15.06) * mm, "end": v(-53.32, 14.04) * mm});
            skLineSegment(sketch, "E33.6.25.0", {"start": v(-53.91, 15.06) * mm, "end": v(-54.5, 16.08) * mm});
            skLineSegment(sketch, "E33.9.25.0", {"start": v(-54.5, 16.08) * mm, "end": v(-56.45, 15.37) * mm});
            skLineSegment(sketch, "E33.2.26.0", {"start": v(-56.82, 19.28) * mm, "end": v(-58.1, 17.65) * mm});
            skLineSegment(sketch, "E33.3.26.0", {"start": v(-57.61, 20.16) * mm, "end": v(-56.82, 19.28) * mm});
            skLineSegment(sketch, "E33.6.26.0", {"start": v(-57.61, 20.16) * mm, "end": v(-58.4, 21.03) * mm});
            skLineSegment(sketch, "E33.9.26.0", {"start": v(-58.4, 21.03) * mm, "end": v(-60.16, 19.93) * mm});
            skLineSegment(sketch, "E33.2.27.0", {"start": v(-61.34, 23.68) * mm, "end": v(-62.25, 21.82) * mm});
            skLineSegment(sketch, "E33.3.27.0", {"start": v(-62.3, 24.37) * mm, "end": v(-61.34, 23.68) * mm});
            skLineSegment(sketch, "E33.6.27.0", {"start": v(-62.3, 24.37) * mm, "end": v(-63.25, 25.06) * mm});
            skLineSegment(sketch, "E33.9.27.0", {"start": v(-63.25, 25.06) * mm, "end": v(-64.74, 23.62) * mm});
            skLineSegment(sketch, "E33.2.28.0", {"start": v(-66.67, 27.04) * mm, "end": v(-67.17, 25.03) * mm});
            skLineSegment(sketch, "E33.3.28.0", {"start": v(-67.75, 27.52) * mm, "end": v(-66.67, 27.04) * mm});
            skLineSegment(sketch, "E33.6.28.0", {"start": v(-67.75, 27.52) * mm, "end": v(-68.82, 28) * mm});
            skLineSegment(sketch, "E33.9.28.0", {"start": v(-68.82, 28) * mm, "end": v(-69.98, 26.28) * mm});
            skLineSegment(sketch, "E33.2.29.0", {"start": v(-72.58, 29.22) * mm, "end": v(-72.66, 27.15) * mm});
            skLineSegment(sketch, "E33.3.29.0", {"start": v(-73.74, 29.47) * mm, "end": v(-72.58, 29.22) * mm});
            skLineSegment(sketch, "E33.6.29.0", {"start": v(-73.74, 29.47) * mm, "end": v(-74.89, 29.71) * mm});
            skLineSegment(sketch, "E33.9.29.0", {"start": v(-74.89, 29.71) * mm, "end": v(-75.67, 27.79) * mm});
            skLineSegment(sketch, "E34.1.0", {"start": v(74.89, 29.71) * mm, "end": v(75.67, 27.79) * mm});
            skLineSegment(sketch, "E34.1.1", {"start": v(73.74, 29.47) * mm, "end": v(74.89, 29.71) * mm});
            skLineSegment(sketch, "E34.1.2", {"start": v(73.74, 29.47) * mm, "end": v(72.58, 29.22) * mm});
            skLineSegment(sketch, "E34.1.3", {"start": v(72.58, 29.22) * mm, "end": v(72.66, 27.15) * mm});
            skLineSegment(sketch, "E34.2.0", {"start": v(68.82, 28) * mm, "end": v(69.98, 26.28) * mm});
            skLineSegment(sketch, "E34.2.1", {"start": v(67.75, 27.52) * mm, "end": v(68.82, 28) * mm});
            skLineSegment(sketch, "E34.2.2", {"start": v(67.75, 27.52) * mm, "end": v(66.67, 27.04) * mm});
            skLineSegment(sketch, "E34.2.3", {"start": v(66.67, 27.04) * mm, "end": v(67.17, 25.03) * mm});
            skLineSegment(sketch, "E35.2.3.0", {"start": v(63.25, 25.06) * mm, "end": v(64.74, 23.62) * mm});
            skLineSegment(sketch, "E35.3.3.0", {"start": v(62.3, 24.37) * mm, "end": v(63.25, 25.06) * mm});
            skLineSegment(sketch, "E35.6.3.0", {"start": v(62.3, 24.37) * mm, "end": v(61.34, 23.68) * mm});
            skLineSegment(sketch, "E35.9.3.0", {"start": v(61.34, 23.68) * mm, "end": v(62.25, 21.82) * mm});
            skLineSegment(sketch, "E35.2.4.0", {"start": v(58.4, 21.03) * mm, "end": v(60.16, 19.93) * mm});
            skLineSegment(sketch, "E35.3.4.0", {"start": v(57.61, 20.16) * mm, "end": v(58.4, 21.03) * mm});
            skLineSegment(sketch, "E35.6.4.0", {"start": v(57.61, 20.16) * mm, "end": v(56.82, 19.28) * mm});
            skLineSegment(sketch, "E35.9.4.0", {"start": v(56.82, 19.28) * mm, "end": v(58.1, 17.65) * mm});
            skLineSegment(sketch, "E35.2.5.0", {"start": v(54.5, 16.08) * mm, "end": v(56.45, 15.37) * mm});
            skLineSegment(sketch, "E35.3.5.0", {"start": v(53.91, 15.06) * mm, "end": v(54.5, 16.08) * mm});
            skLineSegment(sketch, "E35.6.5.0", {"start": v(53.91, 15.06) * mm, "end": v(53.32, 14.04) * mm});
            skLineSegment(sketch, "E35.9.5.0", {"start": v(53.32, 14.04) * mm, "end": v(54.91, 12.7) * mm});
            skLineSegment(sketch, "E35.2.6.0", {"start": v(51.71, 10.43) * mm, "end": v(53.77, 10.14) * mm});
            skLineSegment(sketch, "E35.3.6.0", {"start": v(51.35, 9.3) * mm, "end": v(51.71, 10.43) * mm});
            skLineSegment(sketch, "E35.6.6.0", {"start": v(51.35, 9.3) * mm, "end": v(50.99, 8.19) * mm});
            skLineSegment(sketch, "E35.9.6.0", {"start": v(50.99, 8.19) * mm, "end": v(52.82, 7.22) * mm});
            skLineSegment(sketch, "E35.2.7.0", {"start": v(50.16, 4.32) * mm, "end": v(52.23, 4.47) * mm});
            skLineSegment(sketch, "E35.3.7.0", {"start": v(50.04, 3.15) * mm, "end": v(50.16, 4.32) * mm});
            skLineSegment(sketch, "E35.6.7.0", {"start": v(50.04, 3.15) * mm, "end": v(49.92, 1.98) * mm});
            skLineSegment(sketch, "E35.9.7.0", {"start": v(49.92, 1.98) * mm, "end": v(51.91, 1.4) * mm});
            skLineSegment(sketch, "E35.2.8.0", {"start": v(49.92, -1.98) * mm, "end": v(51.91, -1.4) * mm});
            skLineSegment(sketch, "E35.3.8.0", {"start": v(50.04, -3.15) * mm, "end": v(49.92, -1.98) * mm});
            skLineSegment(sketch, "E35.6.8.0", {"start": v(50.04, -3.15) * mm, "end": v(50.16, -4.32) * mm});
            skLineSegment(sketch, "E35.9.8.0", {"start": v(50.16, -4.32) * mm, "end": v(52.23, -4.47) * mm});
            skLineSegment(sketch, "E35.2.9.0", {"start": v(50.99, -8.19) * mm, "end": v(52.82, -7.22) * mm});
            skLineSegment(sketch, "E35.3.9.0", {"start": v(51.35, -9.3) * mm, "end": v(50.99, -8.19) * mm});
            skLineSegment(sketch, "E35.6.9.0", {"start": v(51.35, -9.3) * mm, "end": v(51.71, -10.43) * mm});
            skLineSegment(sketch, "E35.9.9.0", {"start": v(51.71, -10.43) * mm, "end": v(53.77, -10.14) * mm});
            skLineSegment(sketch, "E35.2.10.0", {"start": v(53.32, -14.04) * mm, "end": v(54.91, -12.7) * mm});
            skLineSegment(sketch, "E35.3.10.0", {"start": v(53.91, -15.06) * mm, "end": v(53.32, -14.04) * mm});
            skLineSegment(sketch, "E35.6.10.0", {"start": v(53.91, -15.06) * mm, "end": v(54.5, -16.08) * mm});
            skLineSegment(sketch, "E35.9.10.0", {"start": v(54.5, -16.08) * mm, "end": v(56.45, -15.37) * mm});
            skLineSegment(sketch, "E35.2.11.0", {"start": v(56.82, -19.28) * mm, "end": v(58.1, -17.65) * mm});
            skLineSegment(sketch, "E35.3.11.0", {"start": v(57.61, -20.16) * mm, "end": v(56.82, -19.28) * mm});
            skLineSegment(sketch, "E35.6.11.0", {"start": v(57.61, -20.16) * mm, "end": v(58.4, -21.03) * mm});
            skLineSegment(sketch, "E35.9.11.0", {"start": v(58.4, -21.03) * mm, "end": v(60.16, -19.93) * mm});
            skLineSegment(sketch, "E35.2.12.0", {"start": v(61.34, -23.68) * mm, "end": v(62.25, -21.82) * mm});
            skLineSegment(sketch, "E35.3.12.0", {"start": v(62.3, -24.37) * mm, "end": v(61.34, -23.68) * mm});
            skLineSegment(sketch, "E35.6.12.0", {"start": v(62.3, -24.37) * mm, "end": v(63.25, -25.06) * mm});
            skLineSegment(sketch, "E35.9.12.0", {"start": v(63.25, -25.06) * mm, "end": v(64.74, -23.62) * mm});
            skLineSegment(sketch, "E35.2.13.0", {"start": v(66.67, -27.04) * mm, "end": v(67.17, -25.03) * mm});
            skLineSegment(sketch, "E35.3.13.0", {"start": v(67.75, -27.52) * mm, "end": v(66.67, -27.04) * mm});
            skLineSegment(sketch, "E35.6.13.0", {"start": v(67.75, -27.52) * mm, "end": v(68.82, -28) * mm});
            skLineSegment(sketch, "E35.9.13.0", {"start": v(68.82, -28) * mm, "end": v(69.98, -26.28) * mm});
            skLineSegment(sketch, "E35.2.14.0", {"start": v(72.58, -29.22) * mm, "end": v(72.66, -27.15) * mm});
            skLineSegment(sketch, "E35.3.14.0", {"start": v(73.74, -29.47) * mm, "end": v(72.58, -29.22) * mm});
            skLineSegment(sketch, "E35.6.14.0", {"start": v(73.74, -29.47) * mm, "end": v(74.89, -29.71) * mm});
            skLineSegment(sketch, "E35.9.14.0", {"start": v(74.89, -29.71) * mm, "end": v(75.67, -27.79) * mm});
            skLineSegment(sketch, "E35.2.15.0", {"start": v(78.82, -30.13) * mm, "end": v(78.46, -28.08) * mm});
            skLineSegment(sketch, "E35.3.15.0", {"start": v(80, -30.13) * mm, "end": v(78.82, -30.13) * mm});
            skLineSegment(sketch, "E35.6.15.0", {"start": v(80, -30.13) * mm, "end": v(81.18, -30.13) * mm});
            skLineSegment(sketch, "E35.9.15.0", {"start": v(81.18, -30.13) * mm, "end": v(81.54, -28.08) * mm});
            skLineSegment(sketch, "E35.2.16.0", {"start": v(85.11, -29.71) * mm, "end": v(84.33, -27.79) * mm});
            skLineSegment(sketch, "E35.3.16.0", {"start": v(86.26, -29.47) * mm, "end": v(85.11, -29.71) * mm});
            skLineSegment(sketch, "E35.6.16.0", {"start": v(86.26, -29.47) * mm, "end": v(87.42, -29.22) * mm});
            skLineSegment(sketch, "E35.9.16.0", {"start": v(87.42, -29.22) * mm, "end": v(87.34, -27.15) * mm});
            skLineSegment(sketch, "E35.2.17.0", {"start": v(91.18, -28) * mm, "end": v(90.02, -26.28) * mm});
            skLineSegment(sketch, "E35.3.17.0", {"start": v(92.25, -27.52) * mm, "end": v(91.18, -28) * mm});
            skLineSegment(sketch, "E35.6.17.0", {"start": v(92.25, -27.52) * mm, "end": v(93.33, -27.04) * mm});
            skLineSegment(sketch, "E35.9.17.0", {"start": v(93.33, -27.04) * mm, "end": v(92.83, -25.03) * mm});
            skLineSegment(sketch, "E35.2.18.0", {"start": v(96.75, -25.06) * mm, "end": v(95.26, -23.62) * mm});
            skLineSegment(sketch, "E35.3.18.0", {"start": v(97.7, -24.37) * mm, "end": v(96.75, -25.06) * mm});
            skLineSegment(sketch, "E35.6.18.0", {"start": v(97.7, -24.37) * mm, "end": v(98.66, -23.68) * mm});
            skLineSegment(sketch, "E35.9.18.0", {"start": v(98.66, -23.68) * mm, "end": v(97.75, -21.82) * mm});
            skLineSegment(sketch, "E35.2.19.0", {"start": v(101.6, -21.03) * mm, "end": v(99.84, -19.93) * mm});
            skLineSegment(sketch, "E35.3.19.0", {"start": v(102.39, -20.16) * mm, "end": v(101.6, -21.03) * mm});
            skLineSegment(sketch, "E35.6.19.0", {"start": v(102.39, -20.16) * mm, "end": v(103.18, -19.28) * mm});
            skLineSegment(sketch, "E35.9.19.0", {"start": v(103.18, -19.28) * mm, "end": v(101.9, -17.65) * mm});
            skLineSegment(sketch, "E35.2.20.0", {"start": v(105.5, -16.08) * mm, "end": v(103.55, -15.37) * mm});
            skLineSegment(sketch, "E35.3.20.0", {"start": v(106.09, -15.06) * mm, "end": v(105.5, -16.08) * mm});
            skLineSegment(sketch, "E35.6.20.0", {"start": v(106.09, -15.06) * mm, "end": v(106.68, -14.04) * mm});
            skLineSegment(sketch, "E35.9.20.0", {"start": v(106.68, -14.04) * mm, "end": v(105.09, -12.7) * mm});
            skLineSegment(sketch, "E35.2.21.0", {"start": v(108.29, -10.43) * mm, "end": v(106.23, -10.14) * mm});
            skLineSegment(sketch, "E35.3.21.0", {"start": v(108.65, -9.3) * mm, "end": v(108.29, -10.43) * mm});
            skLineSegment(sketch, "E35.6.21.0", {"start": v(108.65, -9.3) * mm, "end": v(109.01, -8.19) * mm});
            skLineSegment(sketch, "E35.9.21.0", {"start": v(109.01, -8.19) * mm, "end": v(107.18, -7.22) * mm});
            skLineSegment(sketch, "E35.2.22.0", {"start": v(109.84, -4.32) * mm, "end": v(107.77, -4.47) * mm});
            skLineSegment(sketch, "E35.3.22.0", {"start": v(109.96, -3.15) * mm, "end": v(109.84, -4.32) * mm});
            skLineSegment(sketch, "E35.6.22.0", {"start": v(109.96, -3.15) * mm, "end": v(110.08, -1.98) * mm});
            skLineSegment(sketch, "E35.9.22.0", {"start": v(110.08, -1.98) * mm, "end": v(108.09, -1.4) * mm});
            skLineSegment(sketch, "E35.2.23.0", {"start": v(110.08, 1.98) * mm, "end": v(108.09, 1.4) * mm});
            skLineSegment(sketch, "E35.3.23.0", {"start": v(109.96, 3.15) * mm, "end": v(110.08, 1.98) * mm});
            skLineSegment(sketch, "E35.6.23.0", {"start": v(109.96, 3.15) * mm, "end": v(109.84, 4.32) * mm});
            skLineSegment(sketch, "E35.9.23.0", {"start": v(109.84, 4.32) * mm, "end": v(107.77, 4.47) * mm});
            skLineSegment(sketch, "E35.2.24.0", {"start": v(109.01, 8.19) * mm, "end": v(107.18, 7.22) * mm});
            skLineSegment(sketch, "E35.3.24.0", {"start": v(108.65, 9.3) * mm, "end": v(109.01, 8.19) * mm});
            skLineSegment(sketch, "E35.6.24.0", {"start": v(108.65, 9.3) * mm, "end": v(108.29, 10.43) * mm});
            skLineSegment(sketch, "E35.9.24.0", {"start": v(108.29, 10.43) * mm, "end": v(106.23, 10.14) * mm});
            skLineSegment(sketch, "E35.2.25.0", {"start": v(106.68, 14.04) * mm, "end": v(105.09, 12.7) * mm});
            skLineSegment(sketch, "E35.3.25.0", {"start": v(106.09, 15.06) * mm, "end": v(106.68, 14.04) * mm});
            skLineSegment(sketch, "E35.6.25.0", {"start": v(106.09, 15.06) * mm, "end": v(105.5, 16.08) * mm});
            skLineSegment(sketch, "E35.9.25.0", {"start": v(105.5, 16.08) * mm, "end": v(103.55, 15.37) * mm});
            skLineSegment(sketch, "E35.2.26.0", {"start": v(103.18, 19.28) * mm, "end": v(101.9, 17.65) * mm});
            skLineSegment(sketch, "E35.3.26.0", {"start": v(102.39, 20.16) * mm, "end": v(103.18, 19.28) * mm});
            skLineSegment(sketch, "E35.6.26.0", {"start": v(102.39, 20.16) * mm, "end": v(101.6, 21.03) * mm});
            skLineSegment(sketch, "E35.9.26.0", {"start": v(101.6, 21.03) * mm, "end": v(99.84, 19.93) * mm});
            skLineSegment(sketch, "E35.2.27.0", {"start": v(98.66, 23.68) * mm, "end": v(97.75, 21.82) * mm});
            skLineSegment(sketch, "E35.3.27.0", {"start": v(97.7, 24.37) * mm, "end": v(98.66, 23.68) * mm});
            skLineSegment(sketch, "E35.6.27.0", {"start": v(97.7, 24.37) * mm, "end": v(96.75, 25.06) * mm});
            skLineSegment(sketch, "E35.9.27.0", {"start": v(96.75, 25.06) * mm, "end": v(95.26, 23.62) * mm});
            skLineSegment(sketch, "E35.2.28.0", {"start": v(93.33, 27.04) * mm, "end": v(92.83, 25.03) * mm});
            skLineSegment(sketch, "E35.3.28.0", {"start": v(92.25, 27.52) * mm, "end": v(93.33, 27.04) * mm});
            skLineSegment(sketch, "E35.6.28.0", {"start": v(92.25, 27.52) * mm, "end": v(91.18, 28) * mm});
            skLineSegment(sketch, "E35.9.28.0", {"start": v(91.18, 28) * mm, "end": v(90.02, 26.28) * mm});
            skLineSegment(sketch, "E35.2.29.0", {"start": v(87.42, 29.22) * mm, "end": v(87.34, 27.15) * mm});
            skLineSegment(sketch, "E35.3.29.0", {"start": v(86.26, 29.47) * mm, "end": v(87.42, 29.22) * mm});
            skLineSegment(sketch, "E35.6.29.0", {"start": v(86.26, 29.47) * mm, "end": v(85.11, 29.71) * mm});
            skLineSegment(sketch, "E35.9.29.0", {"start": v(85.11, 29.71) * mm, "end": v(84.33, 27.79) * mm});
            skSolve(sketch);
        }
        {
            var Q0;
            Q0 = qSketchRegion(id + "F2", true);
            extrude(context, id + "F3", {"entities" : qUnion([Q0]), "endBound" : BoundingType.SYMMETRIC, "depth" : 4 * mm, "offsetDistance" : 25 * mm});
        }
        {
            var Q0;
            Q0=makeQuery(id+"F1.opExtrude","CAP_FACE",FACE,{"disambiguationData":[OSD([sQuery(id+"F0.wireOp",EDGE,"E0"),sQuery(id+"F0.wireOp",EDGE,"E1"),sQuery(id+"F0.wireOp",EDGE,"E2"),sQuery(id+"F0.wireOp",EDGE,"E3.MirrorCS"),sQuery(id+"F0.wireOp",EDGE,"E4.MirrorCS"),sQuery(id+"F0.wireOp",EDGE,"E5.1.0"),sQuery(id+"F0.wireOp",EDGE,"E5.1.1"),sQuery(id+"F0.wireOp",EDGE,"E5.1.2"),sQuery(id+"F0.wireOp",EDGE,"E5.1.3"),sQuery(id+"F0.wireOp",EDGE,"E5.2.0"),sQuery(id+"F0.wireOp",EDGE,"E5.2.1"),sQuery(id+"F0.wireOp",EDGE,"E5.2.2"),sQuery(id+"F0.wireOp",EDGE,"E5.2.3"),sQuery(id+"F0.wireOp",EDGE,"E6.1.3.0"),sQuery(id+"F0.wireOp",EDGE,"E6.3.3.0"),sQuery(id+"F0.wireOp",EDGE,"E6.6.3.0"),sQuery(id+"F0.wireOp",EDGE,"E6.9.3.0"),sQuery(id+"F0.wireOp",EDGE,"E6.1.4.0"),sQuery(id+"F0.wireOp",EDGE,"E6.3.4.0"),sQuery(id+"F0.wireOp",EDGE,"E6.6.4.0"),sQuery(id+"F0.wireOp",EDGE,"E6.9.4.0"),sQuery(id+"F0.wireOp",EDGE,"E6.1.5.0"),sQuery(id+"F0.wireOp",EDGE,"E6.3.5.0"),sQuery(id+"F0.wireOp",EDGE,"E6.6.5.0"),sQuery(id+"F0.wireOp",EDGE,"E6.9.5.0"),sQuery(id+"F0.wireOp",EDGE,"E6.1.6.0"),sQuery(id+"F0.wireOp",EDGE,"E6.3.6.0"),sQuery(id+"F0.wireOp",EDGE,"E6.6.6.0"),sQuery(id+"F0.wireOp",EDGE,"E6.9.6.0"),sQuery(id+"F0.wireOp",EDGE,"E6.1.7.0"),sQuery(id+"F0.wireOp",EDGE,"E6.3.7.0"),sQuery(id+"F0.wireOp",EDGE,"E6.6.7.0"),sQuery(id+"F0.wireOp",EDGE,"E6.9.7.0"),sQuery(id+"F0.wireOp",EDGE,"E6.1.8.0"),sQuery(id+"F0.wireOp",EDGE,"E6.3.8.0"),sQuery(id+"F0.wireOp",EDGE,"E6.6.8.0"),sQuery(id+"F0.wireOp",EDGE,"E6.9.8.0"),sQuery(id+"F0.wireOp",EDGE,"E6.1.9.0"),sQuery(id+"F0.wireOp",EDGE,"E6.3.9.0"),sQuery(id+"F0.wireOp",EDGE,"E6.6.9.0"),sQuery(id+"F0.wireOp",EDGE,"E6.9.9.0"),sQuery(id+"F0.wireOp",EDGE,"E7.1.10.0"),sQuery(id+"F0.wireOp",EDGE,"E7.3.10.0"),sQuery(id+"F0.wireOp",EDGE,"E7.6.10.0"),sQuery(id+"F0.wireOp",EDGE,"E7.9.10.0"),sQuery(id+"F0.wireOp",EDGE,"E7.1.11.0"),sQuery(id+"F0.wireOp",EDGE,"E7.3.11.0"),sQuery(id+"F0.wireOp",EDGE,"E7.6.11.0"),sQuery(id+"F0.wireOp",EDGE,"E7.9.11.0"),sQuery(id+"F0.wireOp",EDGE,"E7.1.12.0"),sQuery(id+"F0.wireOp",EDGE,"E7.3.12.0"),sQuery(id+"F0.wireOp",EDGE,"E7.6.12.0"),sQuery(id+"F0.wireOp",EDGE,"E7.9.12.0"),sQuery(id+"F0.wireOp",EDGE,"E7.1.13.0"),sQuery(id+"F0.wireOp",EDGE,"E7.3.13.0"),sQuery(id+"F0.wireOp",EDGE,"E7.6.13.0"),sQuery(id+"F0.wireOp",EDGE,"E7.9.13.0"),sQuery(id+"F0.wireOp",EDGE,"E7.1.14.0"),sQuery(id+"F0.wireOp",EDGE,"E7.3.14.0"),sQuery(id+"F0.wireOp",EDGE,"E7.6.14.0"),sQuery(id+"F0.wireOp",EDGE,"E7.9.14.0"),sQuery(id+"F0.wireOp",EDGE,"E7.1.15.0"),sQuery(id+"F0.wireOp",EDGE,"E7.3.15.0"),sQuery(id+"F0.wireOp",EDGE,"E7.6.15.0"),sQuery(id+"F0.wireOp",EDGE,"E7.9.15.0"),sQuery(id+"F0.wireOp",EDGE,"E7.1.16.0"),sQuery(id+"F0.wireOp",EDGE,"E7.3.16.0"),sQuery(id+"F0.wireOp",EDGE,"E7.6.16.0"),sQuery(id+"F0.wireOp",EDGE,"E7.9.16.0"),sQuery(id+"F0.wireOp",EDGE,"E7.1.17.0"),sQuery(id+"F0.wireOp",EDGE,"E7.3.17.0"),sQuery(id+"F0.wireOp",EDGE,"E7.6.17.0"),sQuery(id+"F0.wireOp",EDGE,"E7.9.17.0"),sQuery(id+"F0.wireOp",EDGE,"E7.1.18.0"),sQuery(id+"F0.wireOp",EDGE,"E7.3.18.0"),sQuery(id+"F0.wireOp",EDGE,"E7.6.18.0"),sQuery(id+"F0.wireOp",EDGE,"E7.9.18.0"),sQuery(id+"F0.wireOp",EDGE,"E7.1.19.0"),sQuery(id+"F0.wireOp",EDGE,"E7.3.19.0"),sQuery(id+"F0.wireOp",EDGE,"E7.6.19.0"),sQuery(id+"F0.wireOp",EDGE,"E7.9.19.0"),sQuery(id+"F0.wireOp",EDGE,"E7.1.20.0"),sQuery(id+"F0.wireOp",EDGE,"E7.3.20.0"),sQuery(id+"F0.wireOp",EDGE,"E7.6.20.0"),sQuery(id+"F0.wireOp",EDGE,"E7.9.20.0"),sQuery(id+"F0.wireOp",EDGE,"E7.1.21.0"),sQuery(id+"F0.wireOp",EDGE,"E7.3.21.0"),sQuery(id+"F0.wireOp",EDGE,"E7.6.21.0"),sQuery(id+"F0.wireOp",EDGE,"E7.9.21.0"),sQuery(id+"F0.wireOp",EDGE,"E7.1.22.0"),sQuery(id+"F0.wireOp",EDGE,"E7.3.22.0"),sQuery(id+"F0.wireOp",EDGE,"E7.6.22.0"),sQuery(id+"F0.wireOp",EDGE,"E7.9.22.0"),sQuery(id+"F0.wireOp",EDGE,"E7.1.23.0"),sQuery(id+"F0.wireOp",EDGE,"E7.3.23.0"),sQuery(id+"F0.wireOp",EDGE,"E7.6.23.0"),sQuery(id+"F0.wireOp",EDGE,"E7.9.23.0"),sQuery(id+"F0.wireOp",EDGE,"E7.1.24.0"),sQuery(id+"F0.wireOp",EDGE,"E7.3.24.0"),sQuery(id+"F0.wireOp",EDGE,"E7.6.24.0"),sQuery(id+"F0.wireOp",EDGE,"E7.9.24.0"),sQuery(id+"F0.wireOp",EDGE,"E7.1.25.0"),sQuery(id+"F0.wireOp",EDGE,"E7.3.25.0"),sQuery(id+"F0.wireOp",EDGE,"E7.6.25.0"),sQuery(id+"F0.wireOp",EDGE,"E7.9.25.0"),sQuery(id+"F0.wireOp",EDGE,"E7.1.26.0"),sQuery(id+"F0.wireOp",EDGE,"E7.3.26.0"),sQuery(id+"F0.wireOp",EDGE,"E7.6.26.0"),sQuery(id+"F0.wireOp",EDGE,"E7.9.26.0"),sQuery(id+"F0.wireOp",EDGE,"E7.1.27.0"),sQuery(id+"F0.wireOp",EDGE,"E7.3.27.0"),sQuery(id+"F0.wireOp",EDGE,"E7.6.27.0"),sQuery(id+"F0.wireOp",EDGE,"E7.9.27.0"),sQuery(id+"F0.wireOp",EDGE,"E7.1.28.0"),sQuery(id+"F0.wireOp",EDGE,"E7.3.28.0"),sQuery(id+"F0.wireOp",EDGE,"E7.6.28.0"),sQuery(id+"F0.wireOp",EDGE,"E7.9.28.0"),sQuery(id+"F0.wireOp",EDGE,"E7.1.29.0"),sQuery(id+"F0.wireOp",EDGE,"E7.3.29.0"),sQuery(id+"F0.wireOp",EDGE,"E7.6.29.0"),sQuery(id+"F0.wireOp",EDGE,"E7.9.29.0")])],"isStart":false});
            var sketch = newSketch(context, id + "F4", { "sketchPlane" : qUnion([Q0])});
            skLineSegment(sketch, "E36.bottom", {"start": v(-1.5, 18.63) * mm, "end": v(1.5, 18.63) * mm});
            skLineSegment(sketch, "E36.top", {"start": v(-1.5, 25.63) * mm, "end": v(1.5, 25.63) * mm});
            skLineSegment(sketch, "E36.left", {"start": v(-1.5, 18.63) * mm, "end": v(-1.5, 25.63) * mm});
            skLineSegment(sketch, "E36.right", {"start": v(1.5, 18.63) * mm, "end": v(1.5, 25.63) * mm});
            skPoint(sketch, "E36.middle", {"position": v(0, 22.13) * mm});
            skLineSegment(sketch, "E37.1.0", {"start": v(-14.11, 21.44) * mm, "end": v(-11.51, 22.94) * mm});
            skLineSegment(sketch, "E37.1.1", {"start": v(-10.61, 15.38) * mm, "end": v(-14.11, 21.44) * mm});
            skLineSegment(sketch, "E37.1.2", {"start": v(-8.01, 16.88) * mm, "end": v(-11.51, 22.94) * mm});
            skLineSegment(sketch, "E37.1.3", {"start": v(-10.61, 15.38) * mm, "end": v(-8.01, 16.88) * mm});
            skLineSegment(sketch, "E37.2.0", {"start": v(-22.94, 11.51) * mm, "end": v(-21.44, 14.11) * mm});
            skLineSegment(sketch, "E37.2.1", {"start": v(-16.88, 8.01) * mm, "end": v(-22.94, 11.51) * mm});
            skLineSegment(sketch, "E37.2.2", {"start": v(-15.38, 10.61) * mm, "end": v(-21.44, 14.11) * mm});
            skLineSegment(sketch, "E37.2.3", {"start": v(-16.88, 8.01) * mm, "end": v(-15.38, 10.61) * mm});
            skPoint(sketch, "E37.center", {"position": v(0, 0) * mm});
            skLineSegment(sketch, "E38.1.3.0", {"start": v(-25.63, -1.5) * mm, "end": v(-25.63, 1.5) * mm});
            skLineSegment(sketch, "E38.3.3.0", {"start": v(-18.63, -1.5) * mm, "end": v(-25.63, -1.5) * mm});
            skLineSegment(sketch, "E38.6.3.0", {"start": v(-18.63, 1.5) * mm, "end": v(-25.63, 1.5) * mm});
            skLineSegment(sketch, "E38.9.3.0", {"start": v(-18.63, -1.5) * mm, "end": v(-18.63, 1.5) * mm});
            skLineSegment(sketch, "E38.1.4.0", {"start": v(-21.44, -14.11) * mm, "end": v(-22.94, -11.51) * mm});
            skLineSegment(sketch, "E38.3.4.0", {"start": v(-15.38, -10.61) * mm, "end": v(-21.44, -14.11) * mm});
            skLineSegment(sketch, "E38.6.4.0", {"start": v(-16.88, -8.01) * mm, "end": v(-22.94, -11.51) * mm});
            skLineSegment(sketch, "E38.9.4.0", {"start": v(-15.38, -10.61) * mm, "end": v(-16.88, -8.01) * mm});
            skLineSegment(sketch, "E38.1.5.0", {"start": v(-11.51, -22.94) * mm, "end": v(-14.11, -21.44) * mm});
            skLineSegment(sketch, "E38.3.5.0", {"start": v(-8.01, -16.88) * mm, "end": v(-11.51, -22.94) * mm});
            skLineSegment(sketch, "E38.6.5.0", {"start": v(-10.61, -15.38) * mm, "end": v(-14.11, -21.44) * mm});
            skLineSegment(sketch, "E38.9.5.0", {"start": v(-8.01, -16.88) * mm, "end": v(-10.61, -15.38) * mm});
            skLineSegment(sketch, "E38.1.6.0", {"start": v(1.5, -25.63) * mm, "end": v(-1.5, -25.63) * mm});
            skLineSegment(sketch, "E38.3.6.0", {"start": v(1.5, -18.63) * mm, "end": v(1.5, -25.63) * mm});
            skLineSegment(sketch, "E38.6.6.0", {"start": v(-1.5, -18.63) * mm, "end": v(-1.5, -25.63) * mm});
            skLineSegment(sketch, "E38.9.6.0", {"start": v(1.5, -18.63) * mm, "end": v(-1.5, -18.63) * mm});
            skLineSegment(sketch, "E38.1.7.0", {"start": v(14.11, -21.44) * mm, "end": v(11.51, -22.94) * mm});
            skLineSegment(sketch, "E38.3.7.0", {"start": v(10.61, -15.38) * mm, "end": v(14.11, -21.44) * mm});
            skLineSegment(sketch, "E38.6.7.0", {"start": v(8.01, -16.88) * mm, "end": v(11.51, -22.94) * mm});
            skLineSegment(sketch, "E38.9.7.0", {"start": v(10.61, -15.38) * mm, "end": v(8.01, -16.88) * mm});
            skLineSegment(sketch, "E38.1.8.0", {"start": v(22.94, -11.51) * mm, "end": v(21.44, -14.11) * mm});
            skLineSegment(sketch, "E38.3.8.0", {"start": v(16.88, -8.01) * mm, "end": v(22.94, -11.51) * mm});
            skLineSegment(sketch, "E38.6.8.0", {"start": v(15.38, -10.61) * mm, "end": v(21.44, -14.11) * mm});
            skLineSegment(sketch, "E38.9.8.0", {"start": v(16.88, -8.01) * mm, "end": v(15.38, -10.61) * mm});
            skLineSegment(sketch, "E38.1.9.0", {"start": v(25.63, 1.5) * mm, "end": v(25.63, -1.5) * mm});
            skLineSegment(sketch, "E38.3.9.0", {"start": v(18.63, 1.5) * mm, "end": v(25.63, 1.5) * mm});
            skLineSegment(sketch, "E38.6.9.0", {"start": v(18.63, -1.5) * mm, "end": v(25.63, -1.5) * mm});
            skLineSegment(sketch, "E38.9.9.0", {"start": v(18.63, 1.5) * mm, "end": v(18.63, -1.5) * mm});
            skLineSegment(sketch, "E38.1.10.0", {"start": v(21.44, 14.11) * mm, "end": v(22.94, 11.51) * mm});
            skLineSegment(sketch, "E38.3.10.0", {"start": v(15.38, 10.61) * mm, "end": v(21.44, 14.11) * mm});
            skLineSegment(sketch, "E38.6.10.0", {"start": v(16.88, 8.01) * mm, "end": v(22.94, 11.51) * mm});
            skLineSegment(sketch, "E38.9.10.0", {"start": v(15.38, 10.61) * mm, "end": v(16.88, 8.01) * mm});
            skLineSegment(sketch, "E38.1.11.0", {"start": v(11.51, 22.94) * mm, "end": v(14.11, 21.44) * mm});
            skLineSegment(sketch, "E38.3.11.0", {"start": v(8.01, 16.88) * mm, "end": v(11.51, 22.94) * mm});
            skLineSegment(sketch, "E38.6.11.0", {"start": v(10.61, 15.38) * mm, "end": v(14.11, 21.44) * mm});
            skLineSegment(sketch, "E38.9.11.0", {"start": v(8.01, 16.88) * mm, "end": v(10.61, 15.38) * mm});
            skSolve(sketch);
        }
        {
            var Q0;
            Q0 = qSketchRegion(id + "F4", true);
            extrude(context, id + "F5", {"entities" : qUnion([Q0]), "operationType" : NewBodyOperationType.REMOVE, "oppositeDirection" : true, "depth" : 2 * mm, "offsetDistance" : 25 * mm});
        }
        {
            var Q0;
            Q0=makeQuery(id+"F5.boolean.opBoolean","COPY",FACE,{"derivedFrom":makeQuery(id+"F5.opExtrude","CAP_FACE",FACE,{"disambiguationData":[OSD([sQuery(id+"F4.wireOp",EDGE,"E36.bottom"),sQuery(id+"F4.wireOp",EDGE,"E36.top"),sQuery(id+"F4.wireOp",EDGE,"E36.left"),sQuery(id+"F4.wireOp",EDGE,"E36.right")])],"isStart":false})});
            extrude(context, id + "F6", {"entities" : qUnion([Q0]), "depth" : 3 * mm, "offsetDistance" : 25 * mm});
        }
        {
            var Q0;
            Q0=makeQuery(id+"F1.opExtrude","CAP_FACE",FACE,{"disambiguationData":[OSD([sQuery(id+"F0.wireOp",EDGE,"E0"),sQuery(id+"F0.wireOp",EDGE,"E1"),sQuery(id+"F0.wireOp",EDGE,"E2"),sQuery(id+"F0.wireOp",EDGE,"E3.MirrorCS"),sQuery(id+"F0.wireOp",EDGE,"E4.MirrorCS"),sQuery(id+"F0.wireOp",EDGE,"E5.1.0"),sQuery(id+"F0.wireOp",EDGE,"E5.1.1"),sQuery(id+"F0.wireOp",EDGE,"E5.1.2"),sQuery(id+"F0.wireOp",EDGE,"E5.1.3"),sQuery(id+"F0.wireOp",EDGE,"E5.2.0"),sQuery(id+"F0.wireOp",EDGE,"E5.2.1"),sQuery(id+"F0.wireOp",EDGE,"E5.2.2"),sQuery(id+"F0.wireOp",EDGE,"E5.2.3"),sQuery(id+"F0.wireOp",EDGE,"E6.1.3.0"),sQuery(id+"F0.wireOp",EDGE,"E6.3.3.0"),sQuery(id+"F0.wireOp",EDGE,"E6.6.3.0"),sQuery(id+"F0.wireOp",EDGE,"E6.9.3.0"),sQuery(id+"F0.wireOp",EDGE,"E6.1.4.0"),sQuery(id+"F0.wireOp",EDGE,"E6.3.4.0"),sQuery(id+"F0.wireOp",EDGE,"E6.6.4.0"),sQuery(id+"F0.wireOp",EDGE,"E6.9.4.0"),sQuery(id+"F0.wireOp",EDGE,"E6.1.5.0"),sQuery(id+"F0.wireOp",EDGE,"E6.3.5.0"),sQuery(id+"F0.wireOp",EDGE,"E6.6.5.0"),sQuery(id+"F0.wireOp",EDGE,"E6.9.5.0"),sQuery(id+"F0.wireOp",EDGE,"E6.1.6.0"),sQuery(id+"F0.wireOp",EDGE,"E6.3.6.0"),sQuery(id+"F0.wireOp",EDGE,"E6.6.6.0"),sQuery(id+"F0.wireOp",EDGE,"E6.9.6.0"),sQuery(id+"F0.wireOp",EDGE,"E6.1.7.0"),sQuery(id+"F0.wireOp",EDGE,"E6.3.7.0"),sQuery(id+"F0.wireOp",EDGE,"E6.6.7.0"),sQuery(id+"F0.wireOp",EDGE,"E6.9.7.0"),sQuery(id+"F0.wireOp",EDGE,"E6.1.8.0"),sQuery(id+"F0.wireOp",EDGE,"E6.3.8.0"),sQuery(id+"F0.wireOp",EDGE,"E6.6.8.0"),sQuery(id+"F0.wireOp",EDGE,"E6.9.8.0"),sQuery(id+"F0.wireOp",EDGE,"E6.1.9.0"),sQuery(id+"F0.wireOp",EDGE,"E6.3.9.0"),sQuery(id+"F0.wireOp",EDGE,"E6.6.9.0"),sQuery(id+"F0.wireOp",EDGE,"E6.9.9.0"),sQuery(id+"F0.wireOp",EDGE,"E7.1.10.0"),sQuery(id+"F0.wireOp",EDGE,"E7.3.10.0"),sQuery(id+"F0.wireOp",EDGE,"E7.6.10.0"),sQuery(id+"F0.wireOp",EDGE,"E7.9.10.0"),sQuery(id+"F0.wireOp",EDGE,"E7.1.11.0"),sQuery(id+"F0.wireOp",EDGE,"E7.3.11.0"),sQuery(id+"F0.wireOp",EDGE,"E7.6.11.0"),sQuery(id+"F0.wireOp",EDGE,"E7.9.11.0"),sQuery(id+"F0.wireOp",EDGE,"E7.1.12.0"),sQuery(id+"F0.wireOp",EDGE,"E7.3.12.0"),sQuery(id+"F0.wireOp",EDGE,"E7.6.12.0"),sQuery(id+"F0.wireOp",EDGE,"E7.9.12.0"),sQuery(id+"F0.wireOp",EDGE,"E7.1.13.0"),sQuery(id+"F0.wireOp",EDGE,"E7.3.13.0"),sQuery(id+"F0.wireOp",EDGE,"E7.6.13.0"),sQuery(id+"F0.wireOp",EDGE,"E7.9.13.0"),sQuery(id+"F0.wireOp",EDGE,"E7.1.14.0"),sQuery(id+"F0.wireOp",EDGE,"E7.3.14.0"),sQuery(id+"F0.wireOp",EDGE,"E7.6.14.0"),sQuery(id+"F0.wireOp",EDGE,"E7.9.14.0"),sQuery(id+"F0.wireOp",EDGE,"E7.1.15.0"),sQuery(id+"F0.wireOp",EDGE,"E7.3.15.0"),sQuery(id+"F0.wireOp",EDGE,"E7.6.15.0"),sQuery(id+"F0.wireOp",EDGE,"E7.9.15.0"),sQuery(id+"F0.wireOp",EDGE,"E7.1.16.0"),sQuery(id+"F0.wireOp",EDGE,"E7.3.16.0"),sQuery(id+"F0.wireOp",EDGE,"E7.6.16.0"),sQuery(id+"F0.wireOp",EDGE,"E7.9.16.0"),sQuery(id+"F0.wireOp",EDGE,"E7.1.17.0"),sQuery(id+"F0.wireOp",EDGE,"E7.3.17.0"),sQuery(id+"F0.wireOp",EDGE,"E7.6.17.0"),sQuery(id+"F0.wireOp",EDGE,"E7.9.17.0"),sQuery(id+"F0.wireOp",EDGE,"E7.1.18.0"),sQuery(id+"F0.wireOp",EDGE,"E7.3.18.0"),sQuery(id+"F0.wireOp",EDGE,"E7.6.18.0"),sQuery(id+"F0.wireOp",EDGE,"E7.9.18.0"),sQuery(id+"F0.wireOp",EDGE,"E7.1.19.0"),sQuery(id+"F0.wireOp",EDGE,"E7.3.19.0"),sQuery(id+"F0.wireOp",EDGE,"E7.6.19.0"),sQuery(id+"F0.wireOp",EDGE,"E7.9.19.0"),sQuery(id+"F0.wireOp",EDGE,"E7.1.20.0"),sQuery(id+"F0.wireOp",EDGE,"E7.3.20.0"),sQuery(id+"F0.wireOp",EDGE,"E7.6.20.0"),sQuery(id+"F0.wireOp",EDGE,"E7.9.20.0"),sQuery(id+"F0.wireOp",EDGE,"E7.1.21.0"),sQuery(id+"F0.wireOp",EDGE,"E7.3.21.0"),sQuery(id+"F0.wireOp",EDGE,"E7.6.21.0"),sQuery(id+"F0.wireOp",EDGE,"E7.9.21.0"),sQuery(id+"F0.wireOp",EDGE,"E7.1.22.0"),sQuery(id+"F0.wireOp",EDGE,"E7.3.22.0"),sQuery(id+"F0.wireOp",EDGE,"E7.6.22.0"),sQuery(id+"F0.wireOp",EDGE,"E7.9.22.0"),sQuery(id+"F0.wireOp",EDGE,"E7.1.23.0"),sQuery(id+"F0.wireOp",EDGE,"E7.3.23.0"),sQuery(id+"F0.wireOp",EDGE,"E7.6.23.0"),sQuery(id+"F0.wireOp",EDGE,"E7.9.23.0"),sQuery(id+"F0.wireOp",EDGE,"E7.1.24.0"),sQuery(id+"F0.wireOp",EDGE,"E7.3.24.0"),sQuery(id+"F0.wireOp",EDGE,"E7.6.24.0"),sQuery(id+"F0.wireOp",EDGE,"E7.9.24.0"),sQuery(id+"F0.wireOp",EDGE,"E7.1.25.0"),sQuery(id+"F0.wireOp",EDGE,"E7.3.25.0"),sQuery(id+"F0.wireOp",EDGE,"E7.6.25.0"),sQuery(id+"F0.wireOp",EDGE,"E7.9.25.0"),sQuery(id+"F0.wireOp",EDGE,"E7.1.26.0"),sQuery(id+"F0.wireOp",EDGE,"E7.3.26.0"),sQuery(id+"F0.wireOp",EDGE,"E7.6.26.0"),sQuery(id+"F0.wireOp",EDGE,"E7.9.26.0"),sQuery(id+"F0.wireOp",EDGE,"E7.1.27.0"),sQuery(id+"F0.wireOp",EDGE,"E7.3.27.0"),sQuery(id+"F0.wireOp",EDGE,"E7.6.27.0"),sQuery(id+"F0.wireOp",EDGE,"E7.9.27.0"),sQuery(id+"F0.wireOp",EDGE,"E7.1.28.0"),sQuery(id+"F0.wireOp",EDGE,"E7.3.28.0"),sQuery(id+"F0.wireOp",EDGE,"E7.6.28.0"),sQuery(id+"F0.wireOp",EDGE,"E7.9.28.0"),sQuery(id+"F0.wireOp",EDGE,"E7.1.29.0"),sQuery(id+"F0.wireOp",EDGE,"E7.3.29.0"),sQuery(id+"F0.wireOp",EDGE,"E7.6.29.0"),sQuery(id+"F0.wireOp",EDGE,"E7.9.29.0")])],"isStart":false});
            var sketch = newSketch(context, id + "F7", { "sketchPlane" : qUnion([Q0])});
            skLineSegment(sketch, "E39.bottom", {"start": v(-1.5, 10.63) * mm, "end": v(1.5, 10.63) * mm});
            skLineSegment(sketch, "E39.top", {"start": v(-1.5, 17.63) * mm, "end": v(1.5, 17.63) * mm});
            skLineSegment(sketch, "E39.left", {"start": v(-1.5, 10.63) * mm, "end": v(-1.5, 17.63) * mm});
            skLineSegment(sketch, "E39.right", {"start": v(1.5, 10.63) * mm, "end": v(1.5, 17.63) * mm});
            skPoint(sketch, "E39.middle", {"position": v(0, 14.13) * mm});
            skSolve(sketch);
        }
        {
            var Q0;
            Q0 = qSketchRegion(id + "F7", true);
            extrude(context, id + "F8", {"entities" : qUnion([Q0]), "operationType" : NewBodyOperationType.REMOVE, "oppositeDirection" : true, "depth" : 2 * mm, "offsetDistance" : 25 * mm});
        }
        {
            var Q0;
            Q0=qCreatedBy(makeId("Top.planeOp"),FACE);
            var sketch = newSketch(context, id + "F9", { "sketchPlane" : qUnion([Q0])});
            skCircle(sketch, "E40", {"center": v(0, 0) * mm, "radius": 2 * mm});
            skCircle(sketch, "E41", {"center": v(-40, 0) * mm, "radius": 2 * mm});
            skCircle(sketch, "E42", {"center": v(-80, 0) * mm, "radius": 2 * mm});
            skCircle(sketch, "E43.MirrorC", {"center": v(40, 0) * mm, "radius": 2 * mm});
            skCircle(sketch, "E44.MirrorC", {"center": v(80, 0) * mm, "radius": 2 * mm});
            skSolve(sketch);
        }
        {
            var Q0;
            Q0 = qSketchRegion(id + "F9", true);
            extrude(context, id + "F10", {"entities" : qUnion([Q0]), "oppositeDirection" : true, "depth" : 25 * mm, "offsetDistance" : 25 * mm});
        }
        {
            var Q0;
            Q0=makeQuery(id+"F10.opExtrude","CAP_FACE",FACE,{"disambiguationData":[OSD([sQuery(id+"F9.wireOp",EDGE,"E40")])],"isStart":false});
            var sketch = newSketch(context, id + "F11", { "sketchPlane" : qUnion([Q0])});
            skLineSegment(sketch, "E45.bottom", {"start": v(-100, -5) * mm, "end": v(100, -5) * mm});
            skLineSegment(sketch, "E45.top", {"start": v(-100, 5) * mm, "end": v(100, 5) * mm});
            skLineSegment(sketch, "E45.left", {"start": v(-100, -5) * mm, "end": v(-100, 5) * mm});
            skLineSegment(sketch, "E45.right", {"start": v(100, -5) * mm, "end": v(100, 5) * mm});
            skPoint(sketch, "E45.middle", {"position": v(0, 0) * mm});
            skSolve(sketch);
        }
        {
            var Q0;
            Q0 = qSketchRegion(id + "F11", true);
            extrude(context, id + "F12", {"entities" : qUnion([Q0]), "endBound" : BoundingType.SYMMETRIC, "depth" : 10 * mm, "offsetDistance" : 25 * mm});
        }
        {
            var Q0;
            Q0=makeQuery(id+"F10.opExtrude","SWEPT_BODY",BODY,{"disambiguationData":[OSD([sQuery(id+"F9.wireOp",EDGE,"E42")])]});
            var Q1;
            Q1=makeQuery(id+"F10.opExtrude","SWEPT_BODY",BODY,{"disambiguationData":[OSD([sQuery(id+"F9.wireOp",EDGE,"E41")])]});
            var Q2;
            Q2=makeQuery(id+"F10.opExtrude","SWEPT_BODY",BODY,{"disambiguationData":[OSD([sQuery(id+"F9.wireOp",EDGE,"E40")])]});
            var Q3;
            Q3=makeQuery(id+"F10.opExtrude","SWEPT_BODY",BODY,{"disambiguationData":[OSD([sQuery(id+"F9.wireOp",EDGE,"E43.MirrorC")])]});
            var Q4;
            Q4=makeQuery(id+"F10.opExtrude","SWEPT_BODY",BODY,{"disambiguationData":[OSD([sQuery(id+"F9.wireOp",EDGE,"E44.MirrorC")])]});
            var Q5;
            Q5=makeQuery(id+"F3.opExtrude","SWEPT_BODY",BODY,{"disambiguationData":[OSD([sQuery(id+"F2.wireOp",EDGE,"E27.MirrorC"),sQuery(id+"F2.wireOp",EDGE,"E28.MirrorCS"),sQuery(id+"F2.wireOp",EDGE,"E29.MirrorCS"),sQuery(id+"F2.wireOp",EDGE,"E30.MirrorCS"),sQuery(id+"F2.wireOp",EDGE,"E31.MirrorCS"),sQuery(id+"F2.wireOp",EDGE,"E34.1.0"),sQuery(id+"F2.wireOp",EDGE,"E34.1.1"),sQuery(id+"F2.wireOp",EDGE,"E34.1.2"),sQuery(id+"F2.wireOp",EDGE,"E34.1.3"),sQuery(id+"F2.wireOp",EDGE,"E34.2.0"),sQuery(id+"F2.wireOp",EDGE,"E34.2.1"),sQuery(id+"F2.wireOp",EDGE,"E34.2.2"),sQuery(id+"F2.wireOp",EDGE,"E34.2.3"),sQuery(id+"F2.wireOp",EDGE,"E35.2.3.0"),sQuery(id+"F2.wireOp",EDGE,"E35.3.3.0"),sQuery(id+"F2.wireOp",EDGE,"E35.6.3.0"),sQuery(id+"F2.wireOp",EDGE,"E35.9.3.0"),sQuery(id+"F2.wireOp",EDGE,"E35.2.4.0"),sQuery(id+"F2.wireOp",EDGE,"E35.3.4.0"),sQuery(id+"F2.wireOp",EDGE,"E35.6.4.0"),sQuery(id+"F2.wireOp",EDGE,"E35.9.4.0"),sQuery(id+"F2.wireOp",EDGE,"E35.2.5.0"),sQuery(id+"F2.wireOp",EDGE,"E35.3.5.0"),sQuery(id+"F2.wireOp",EDGE,"E35.6.5.0"),sQuery(id+"F2.wireOp",EDGE,"E35.9.5.0"),sQuery(id+"F2.wireOp",EDGE,"E35.2.6.0"),sQuery(id+"F2.wireOp",EDGE,"E35.3.6.0"),sQuery(id+"F2.wireOp",EDGE,"E35.6.6.0"),sQuery(id+"F2.wireOp",EDGE,"E35.9.6.0"),sQuery(id+"F2.wireOp",EDGE,"E35.2.7.0"),sQuery(id+"F2.wireOp",EDGE,"E35.3.7.0"),sQuery(id+"F2.wireOp",EDGE,"E35.6.7.0"),sQuery(id+"F2.wireOp",EDGE,"E35.9.7.0"),sQuery(id+"F2.wireOp",EDGE,"E35.2.8.0"),sQuery(id+"F2.wireOp",EDGE,"E35.3.8.0"),sQuery(id+"F2.wireOp",EDGE,"E35.6.8.0"),sQuery(id+"F2.wireOp",EDGE,"E35.9.8.0"),sQuery(id+"F2.wireOp",EDGE,"E35.2.9.0"),sQuery(id+"F2.wireOp",EDGE,"E35.3.9.0"),sQuery(id+"F2.wireOp",EDGE,"E35.6.9.0"),sQuery(id+"F2.wireOp",EDGE,"E35.9.9.0"),sQuery(id+"F2.wireOp",EDGE,"E35.2.10.0"),sQuery(id+"F2.wireOp",EDGE,"E35.3.10.0"),sQuery(id+"F2.wireOp",EDGE,"E35.6.10.0"),sQuery(id+"F2.wireOp",EDGE,"E35.9.10.0"),sQuery(id+"F2.wireOp",EDGE,"E35.2.11.0"),sQuery(id+"F2.wireOp",EDGE,"E35.3.11.0"),sQuery(id+"F2.wireOp",EDGE,"E35.6.11.0"),sQuery(id+"F2.wireOp",EDGE,"E35.9.11.0"),sQuery(id+"F2.wireOp",EDGE,"E35.2.12.0"),sQuery(id+"F2.wireOp",EDGE,"E35.3.12.0"),sQuery(id+"F2.wireOp",EDGE,"E35.6.12.0"),sQuery(id+"F2.wireOp",EDGE,"E35.9.12.0"),sQuery(id+"F2.wireOp",EDGE,"E35.2.13.0"),sQuery(id+"F2.wireOp",EDGE,"E35.3.13.0"),sQuery(id+"F2.wireOp",EDGE,"E35.6.13.0"),sQuery(id+"F2.wireOp",EDGE,"E35.9.13.0"),sQuery(id+"F2.wireOp",EDGE,"E35.2.14.0"),sQuery(id+"F2.wireOp",EDGE,"E35.3.14.0"),sQuery(id+"F2.wireOp",EDGE,"E35.6.14.0"),sQuery(id+"F2.wireOp",EDGE,"E35.9.14.0"),sQuery(id+"F2.wireOp",EDGE,"E35.2.15.0"),sQuery(id+"F2.wireOp",EDGE,"E35.3.15.0"),sQuery(id+"F2.wireOp",EDGE,"E35.6.15.0"),sQuery(id+"F2.wireOp",EDGE,"E35.9.15.0"),sQuery(id+"F2.wireOp",EDGE,"E35.2.16.0"),sQuery(id+"F2.wireOp",EDGE,"E35.3.16.0"),sQuery(id+"F2.wireOp",EDGE,"E35.6.16.0"),sQuery(id+"F2.wireOp",EDGE,"E35.9.16.0"),sQuery(id+"F2.wireOp",EDGE,"E35.2.17.0"),sQuery(id+"F2.wireOp",EDGE,"E35.3.17.0"),sQuery(id+"F2.wireOp",EDGE,"E35.6.17.0"),sQuery(id+"F2.wireOp",EDGE,"E35.9.17.0"),sQuery(id+"F2.wireOp",EDGE,"E35.2.18.0"),sQuery(id+"F2.wireOp",EDGE,"E35.3.18.0"),sQuery(id+"F2.wireOp",EDGE,"E35.6.18.0"),sQuery(id+"F2.wireOp",EDGE,"E35.9.18.0"),sQuery(id+"F2.wireOp",EDGE,"E35.2.19.0"),sQuery(id+"F2.wireOp",EDGE,"E35.3.19.0"),sQuery(id+"F2.wireOp",EDGE,"E35.6.19.0"),sQuery(id+"F2.wireOp",EDGE,"E35.9.19.0"),sQuery(id+"F2.wireOp",EDGE,"E35.2.20.0"),sQuery(id+"F2.wireOp",EDGE,"E35.3.20.0"),sQuery(id+"F2.wireOp",EDGE,"E35.6.20.0"),sQuery(id+"F2.wireOp",EDGE,"E35.9.20.0"),sQuery(id+"F2.wireOp",EDGE,"E35.2.21.0"),sQuery(id+"F2.wireOp",EDGE,"E35.3.21.0"),sQuery(id+"F2.wireOp",EDGE,"E35.6.21.0"),sQuery(id+"F2.wireOp",EDGE,"E35.9.21.0"),sQuery(id+"F2.wireOp",EDGE,"E35.2.22.0"),sQuery(id+"F2.wireOp",EDGE,"E35.3.22.0"),sQuery(id+"F2.wireOp",EDGE,"E35.6.22.0"),sQuery(id+"F2.wireOp",EDGE,"E35.9.22.0"),sQuery(id+"F2.wireOp",EDGE,"E35.2.23.0"),sQuery(id+"F2.wireOp",EDGE,"E35.3.23.0"),sQuery(id+"F2.wireOp",EDGE,"E35.6.23.0"),sQuery(id+"F2.wireOp",EDGE,"E35.9.23.0"),sQuery(id+"F2.wireOp",EDGE,"E35.2.24.0"),sQuery(id+"F2.wireOp",EDGE,"E35.3.24.0"),sQuery(id+"F2.wireOp",EDGE,"E35.6.24.0"),sQuery(id+"F2.wireOp",EDGE,"E35.9.24.0"),sQuery(id+"F2.wireOp",EDGE,"E35.2.25.0"),sQuery(id+"F2.wireOp",EDGE,"E35.3.25.0"),sQuery(id+"F2.wireOp",EDGE,"E35.6.25.0"),sQuery(id+"F2.wireOp",EDGE,"E35.9.25.0"),sQuery(id+"F2.wireOp",EDGE,"E35.2.26.0"),sQuery(id+"F2.wireOp",EDGE,"E35.3.26.0"),sQuery(id+"F2.wireOp",EDGE,"E35.6.26.0"),sQuery(id+"F2.wireOp",EDGE,"E35.9.26.0"),sQuery(id+"F2.wireOp",EDGE,"E35.2.27.0"),sQuery(id+"F2.wireOp",EDGE,"E35.3.27.0"),sQuery(id+"F2.wireOp",EDGE,"E35.6.27.0"),sQuery(id+"F2.wireOp",EDGE,"E35.9.27.0"),sQuery(id+"F2.wireOp",EDGE,"E35.2.28.0"),sQuery(id+"F2.wireOp",EDGE,"E35.3.28.0"),sQuery(id+"F2.wireOp",EDGE,"E35.6.28.0"),sQuery(id+"F2.wireOp",EDGE,"E35.9.28.0"),sQuery(id+"F2.wireOp",EDGE,"E35.2.29.0"),sQuery(id+"F2.wireOp",EDGE,"E35.3.29.0"),sQuery(id+"F2.wireOp",EDGE,"E35.6.29.0"),sQuery(id+"F2.wireOp",EDGE,"E35.9.29.0")])]});
            var Q6;
            Q6=makeQuery(id+"F3.opExtrude","SWEPT_BODY",BODY,{"disambiguationData":[OSD([sQuery(id+"F2.wireOp",EDGE,"E8"),sQuery(id+"F2.wireOp",EDGE,"E9"),sQuery(id+"F2.wireOp",EDGE,"E10"),sQuery(id+"F2.wireOp",EDGE,"E11.MirrorCS"),sQuery(id+"F2.wireOp",EDGE,"E12.MirrorCS"),sQuery(id+"F2.wireOp",EDGE,"E13.1.0"),sQuery(id+"F2.wireOp",EDGE,"E13.1.1"),sQuery(id+"F2.wireOp",EDGE,"E13.1.2"),sQuery(id+"F2.wireOp",EDGE,"E13.1.3"),sQuery(id+"F2.wireOp",EDGE,"E13.2.0"),sQuery(id+"F2.wireOp",EDGE,"E13.2.1"),sQuery(id+"F2.wireOp",EDGE,"E13.2.2"),sQuery(id+"F2.wireOp",EDGE,"E13.2.3"),sQuery(id+"F2.wireOp",EDGE,"E14.2.3.0"),sQuery(id+"F2.wireOp",EDGE,"E14.3.3.0"),sQuery(id+"F2.wireOp",EDGE,"E14.6.3.0"),sQuery(id+"F2.wireOp",EDGE,"E14.9.3.0"),sQuery(id+"F2.wireOp",EDGE,"E14.2.4.0"),sQuery(id+"F2.wireOp",EDGE,"E14.3.4.0"),sQuery(id+"F2.wireOp",EDGE,"E14.6.4.0"),sQuery(id+"F2.wireOp",EDGE,"E14.9.4.0"),sQuery(id+"F2.wireOp",EDGE,"E14.2.5.0"),sQuery(id+"F2.wireOp",EDGE,"E14.3.5.0"),sQuery(id+"F2.wireOp",EDGE,"E14.6.5.0"),sQuery(id+"F2.wireOp",EDGE,"E14.9.5.0"),sQuery(id+"F2.wireOp",EDGE,"E14.2.6.0"),sQuery(id+"F2.wireOp",EDGE,"E14.3.6.0"),sQuery(id+"F2.wireOp",EDGE,"E14.6.6.0"),sQuery(id+"F2.wireOp",EDGE,"E14.9.6.0"),sQuery(id+"F2.wireOp",EDGE,"E14.2.7.0"),sQuery(id+"F2.wireOp",EDGE,"E14.3.7.0"),sQuery(id+"F2.wireOp",EDGE,"E14.6.7.0"),sQuery(id+"F2.wireOp",EDGE,"E14.9.7.0"),sQuery(id+"F2.wireOp",EDGE,"E14.2.8.0"),sQuery(id+"F2.wireOp",EDGE,"E14.3.8.0"),sQuery(id+"F2.wireOp",EDGE,"E14.6.8.0"),sQuery(id+"F2.wireOp",EDGE,"E14.9.8.0"),sQuery(id+"F2.wireOp",EDGE,"E14.2.9.0"),sQuery(id+"F2.wireOp",EDGE,"E14.3.9.0"),sQuery(id+"F2.wireOp",EDGE,"E14.6.9.0"),sQuery(id+"F2.wireOp",EDGE,"E14.9.9.0")])]});
            var Q7;
            Q7=makeQuery(id+"F1.opExtrude","SWEPT_BODY",BODY,{"disambiguationData":[OSD([sQuery(id+"F0.wireOp",EDGE,"E0"),sQuery(id+"F0.wireOp",EDGE,"E1"),sQuery(id+"F0.wireOp",EDGE,"E2"),sQuery(id+"F0.wireOp",EDGE,"E3.MirrorCS"),sQuery(id+"F0.wireOp",EDGE,"E4.MirrorCS"),sQuery(id+"F0.wireOp",EDGE,"E5.1.0"),sQuery(id+"F0.wireOp",EDGE,"E5.1.1"),sQuery(id+"F0.wireOp",EDGE,"E5.1.2"),sQuery(id+"F0.wireOp",EDGE,"E5.1.3"),sQuery(id+"F0.wireOp",EDGE,"E5.2.0"),sQuery(id+"F0.wireOp",EDGE,"E5.2.1"),sQuery(id+"F0.wireOp",EDGE,"E5.2.2"),sQuery(id+"F0.wireOp",EDGE,"E5.2.3"),sQuery(id+"F0.wireOp",EDGE,"E6.1.3.0"),sQuery(id+"F0.wireOp",EDGE,"E6.3.3.0"),sQuery(id+"F0.wireOp",EDGE,"E6.6.3.0"),sQuery(id+"F0.wireOp",EDGE,"E6.9.3.0"),sQuery(id+"F0.wireOp",EDGE,"E6.1.4.0"),sQuery(id+"F0.wireOp",EDGE,"E6.3.4.0"),sQuery(id+"F0.wireOp",EDGE,"E6.6.4.0"),sQuery(id+"F0.wireOp",EDGE,"E6.9.4.0"),sQuery(id+"F0.wireOp",EDGE,"E6.1.5.0"),sQuery(id+"F0.wireOp",EDGE,"E6.3.5.0"),sQuery(id+"F0.wireOp",EDGE,"E6.6.5.0"),sQuery(id+"F0.wireOp",EDGE,"E6.9.5.0"),sQuery(id+"F0.wireOp",EDGE,"E6.1.6.0"),sQuery(id+"F0.wireOp",EDGE,"E6.3.6.0"),sQuery(id+"F0.wireOp",EDGE,"E6.6.6.0"),sQuery(id+"F0.wireOp",EDGE,"E6.9.6.0"),sQuery(id+"F0.wireOp",EDGE,"E6.1.7.0"),sQuery(id+"F0.wireOp",EDGE,"E6.3.7.0"),sQuery(id+"F0.wireOp",EDGE,"E6.6.7.0"),sQuery(id+"F0.wireOp",EDGE,"E6.9.7.0"),sQuery(id+"F0.wireOp",EDGE,"E6.1.8.0"),sQuery(id+"F0.wireOp",EDGE,"E6.3.8.0"),sQuery(id+"F0.wireOp",EDGE,"E6.6.8.0"),sQuery(id+"F0.wireOp",EDGE,"E6.9.8.0"),sQuery(id+"F0.wireOp",EDGE,"E6.1.9.0"),sQuery(id+"F0.wireOp",EDGE,"E6.3.9.0"),sQuery(id+"F0.wireOp",EDGE,"E6.6.9.0"),sQuery(id+"F0.wireOp",EDGE,"E6.9.9.0"),sQuery(id+"F0.wireOp",EDGE,"E7.1.10.0"),sQuery(id+"F0.wireOp",EDGE,"E7.3.10.0"),sQuery(id+"F0.wireOp",EDGE,"E7.6.10.0"),sQuery(id+"F0.wireOp",EDGE,"E7.9.10.0"),sQuery(id+"F0.wireOp",EDGE,"E7.1.11.0"),sQuery(id+"F0.wireOp",EDGE,"E7.3.11.0"),sQuery(id+"F0.wireOp",EDGE,"E7.6.11.0"),sQuery(id+"F0.wireOp",EDGE,"E7.9.11.0"),sQuery(id+"F0.wireOp",EDGE,"E7.1.12.0"),sQuery(id+"F0.wireOp",EDGE,"E7.3.12.0"),sQuery(id+"F0.wireOp",EDGE,"E7.6.12.0"),sQuery(id+"F0.wireOp",EDGE,"E7.9.12.0"),sQuery(id+"F0.wireOp",EDGE,"E7.1.13.0"),sQuery(id+"F0.wireOp",EDGE,"E7.3.13.0"),sQuery(id+"F0.wireOp",EDGE,"E7.6.13.0"),sQuery(id+"F0.wireOp",EDGE,"E7.9.13.0"),sQuery(id+"F0.wireOp",EDGE,"E7.1.14.0"),sQuery(id+"F0.wireOp",EDGE,"E7.3.14.0"),sQuery(id+"F0.wireOp",EDGE,"E7.6.14.0"),sQuery(id+"F0.wireOp",EDGE,"E7.9.14.0"),sQuery(id+"F0.wireOp",EDGE,"E7.1.15.0"),sQuery(id+"F0.wireOp",EDGE,"E7.3.15.0"),sQuery(id+"F0.wireOp",EDGE,"E7.6.15.0"),sQuery(id+"F0.wireOp",EDGE,"E7.9.15.0"),sQuery(id+"F0.wireOp",EDGE,"E7.1.16.0"),sQuery(id+"F0.wireOp",EDGE,"E7.3.16.0"),sQuery(id+"F0.wireOp",EDGE,"E7.6.16.0"),sQuery(id+"F0.wireOp",EDGE,"E7.9.16.0"),sQuery(id+"F0.wireOp",EDGE,"E7.1.17.0"),sQuery(id+"F0.wireOp",EDGE,"E7.3.17.0"),sQuery(id+"F0.wireOp",EDGE,"E7.6.17.0"),sQuery(id+"F0.wireOp",EDGE,"E7.9.17.0"),sQuery(id+"F0.wireOp",EDGE,"E7.1.18.0"),sQuery(id+"F0.wireOp",EDGE,"E7.3.18.0"),sQuery(id+"F0.wireOp",EDGE,"E7.6.18.0"),sQuery(id+"F0.wireOp",EDGE,"E7.9.18.0"),sQuery(id+"F0.wireOp",EDGE,"E7.1.19.0"),sQuery(id+"F0.wireOp",EDGE,"E7.3.19.0"),sQuery(id+"F0.wireOp",EDGE,"E7.6.19.0"),sQuery(id+"F0.wireOp",EDGE,"E7.9.19.0"),sQuery(id+"F0.wireOp",EDGE,"E7.1.20.0"),sQuery(id+"F0.wireOp",EDGE,"E7.3.20.0"),sQuery(id+"F0.wireOp",EDGE,"E7.6.20.0"),sQuery(id+"F0.wireOp",EDGE,"E7.9.20.0"),sQuery(id+"F0.wireOp",EDGE,"E7.1.21.0"),sQuery(id+"F0.wireOp",EDGE,"E7.3.21.0"),sQuery(id+"F0.wireOp",EDGE,"E7.6.21.0"),sQuery(id+"F0.wireOp",EDGE,"E7.9.21.0"),sQuery(id+"F0.wireOp",EDGE,"E7.1.22.0"),sQuery(id+"F0.wireOp",EDGE,"E7.3.22.0"),sQuery(id+"F0.wireOp",EDGE,"E7.6.22.0"),sQuery(id+"F0.wireOp",EDGE,"E7.9.22.0"),sQuery(id+"F0.wireOp",EDGE,"E7.1.23.0"),sQuery(id+"F0.wireOp",EDGE,"E7.3.23.0"),sQuery(id+"F0.wireOp",EDGE,"E7.6.23.0"),sQuery(id+"F0.wireOp",EDGE,"E7.9.23.0"),sQuery(id+"F0.wireOp",EDGE,"E7.1.24.0"),sQuery(id+"F0.wireOp",EDGE,"E7.3.24.0"),sQuery(id+"F0.wireOp",EDGE,"E7.6.24.0"),sQuery(id+"F0.wireOp",EDGE,"E7.9.24.0"),sQuery(id+"F0.wireOp",EDGE,"E7.1.25.0"),sQuery(id+"F0.wireOp",EDGE,"E7.3.25.0"),sQuery(id+"F0.wireOp",EDGE,"E7.6.25.0"),sQuery(id+"F0.wireOp",EDGE,"E7.9.25.0"),sQuery(id+"F0.wireOp",EDGE,"E7.1.26.0"),sQuery(id+"F0.wireOp",EDGE,"E7.3.26.0"),sQuery(id+"F0.wireOp",EDGE,"E7.6.26.0"),sQuery(id+"F0.wireOp",EDGE,"E7.9.26.0"),sQuery(id+"F0.wireOp",EDGE,"E7.1.27.0"),sQuery(id+"F0.wireOp",EDGE,"E7.3.27.0"),sQuery(id+"F0.wireOp",EDGE,"E7.6.27.0"),sQuery(id+"F0.wireOp",EDGE,"E7.9.27.0"),sQuery(id+"F0.wireOp",EDGE,"E7.1.28.0"),sQuery(id+"F0.wireOp",EDGE,"E7.3.28.0"),sQuery(id+"F0.wireOp",EDGE,"E7.6.28.0"),sQuery(id+"F0.wireOp",EDGE,"E7.9.28.0"),sQuery(id+"F0.wireOp",EDGE,"E7.1.29.0"),sQuery(id+"F0.wireOp",EDGE,"E7.3.29.0"),sQuery(id+"F0.wireOp",EDGE,"E7.6.29.0"),sQuery(id+"F0.wireOp",EDGE,"E7.9.29.0")])]});
            var Q8;
            Q8=makeQuery(id+"F3.opExtrude","SWEPT_BODY",BODY,{"disambiguationData":[OSD([sQuery(id+"F2.wireOp",EDGE,"E15.MirrorC"),sQuery(id+"F2.wireOp",EDGE,"E16"),sQuery(id+"F2.wireOp",EDGE,"E17"),sQuery(id+"F2.wireOp",EDGE,"E18.MirrorCS"),sQuery(id+"F2.wireOp",EDGE,"E19.MirrorCS"),sQuery(id+"F2.wireOp",EDGE,"E20.1.0"),sQuery(id+"F2.wireOp",EDGE,"E20.1.1"),sQuery(id+"F2.wireOp",EDGE,"E20.1.2"),sQuery(id+"F2.wireOp",EDGE,"E20.1.3"),sQuery(id+"F2.wireOp",EDGE,"E20.2.0"),sQuery(id+"F2.wireOp",EDGE,"E20.2.1"),sQuery(id+"F2.wireOp",EDGE,"E20.2.2"),sQuery(id+"F2.wireOp",EDGE,"E20.2.3"),sQuery(id+"F2.wireOp",EDGE,"E21.1.3.0"),sQuery(id+"F2.wireOp",EDGE,"E21.3.3.0"),sQuery(id+"F2.wireOp",EDGE,"E21.6.3.0"),sQuery(id+"F2.wireOp",EDGE,"E21.9.3.0"),sQuery(id+"F2.wireOp",EDGE,"E21.1.4.0"),sQuery(id+"F2.wireOp",EDGE,"E21.3.4.0"),sQuery(id+"F2.wireOp",EDGE,"E21.6.4.0"),sQuery(id+"F2.wireOp",EDGE,"E21.9.4.0"),sQuery(id+"F2.wireOp",EDGE,"E21.1.5.0"),sQuery(id+"F2.wireOp",EDGE,"E21.3.5.0"),sQuery(id+"F2.wireOp",EDGE,"E21.6.5.0"),sQuery(id+"F2.wireOp",EDGE,"E21.9.5.0"),sQuery(id+"F2.wireOp",EDGE,"E21.1.6.0"),sQuery(id+"F2.wireOp",EDGE,"E21.3.6.0"),sQuery(id+"F2.wireOp",EDGE,"E21.6.6.0"),sQuery(id+"F2.wireOp",EDGE,"E21.9.6.0"),sQuery(id+"F2.wireOp",EDGE,"E21.1.7.0"),sQuery(id+"F2.wireOp",EDGE,"E21.3.7.0"),sQuery(id+"F2.wireOp",EDGE,"E21.6.7.0"),sQuery(id+"F2.wireOp",EDGE,"E21.9.7.0"),sQuery(id+"F2.wireOp",EDGE,"E21.1.8.0"),sQuery(id+"F2.wireOp",EDGE,"E21.3.8.0"),sQuery(id+"F2.wireOp",EDGE,"E21.6.8.0"),sQuery(id+"F2.wireOp",EDGE,"E21.9.8.0"),sQuery(id+"F2.wireOp",EDGE,"E21.1.9.0"),sQuery(id+"F2.wireOp",EDGE,"E21.3.9.0"),sQuery(id+"F2.wireOp",EDGE,"E21.6.9.0"),sQuery(id+"F2.wireOp",EDGE,"E21.9.9.0")])]});
            var Q9;
            Q9=makeQuery(id+"F3.opExtrude","SWEPT_BODY",BODY,{"disambiguationData":[OSD([sQuery(id+"F2.wireOp",EDGE,"E22"),sQuery(id+"F2.wireOp",EDGE,"E23"),sQuery(id+"F2.wireOp",EDGE,"E24"),sQuery(id+"F2.wireOp",EDGE,"E25"),sQuery(id+"F2.wireOp",EDGE,"E26"),sQuery(id+"F2.wireOp",EDGE,"E32.1.0"),sQuery(id+"F2.wireOp",EDGE,"E32.1.1"),sQuery(id+"F2.wireOp",EDGE,"E32.1.2"),sQuery(id+"F2.wireOp",EDGE,"E32.1.3"),sQuery(id+"F2.wireOp",EDGE,"E32.2.0"),sQuery(id+"F2.wireOp",EDGE,"E32.2.1"),sQuery(id+"F2.wireOp",EDGE,"E32.2.2"),sQuery(id+"F2.wireOp",EDGE,"E32.2.3"),sQuery(id+"F2.wireOp",EDGE,"E33.2.3.0"),sQuery(id+"F2.wireOp",EDGE,"E33.3.3.0"),sQuery(id+"F2.wireOp",EDGE,"E33.6.3.0"),sQuery(id+"F2.wireOp",EDGE,"E33.9.3.0"),sQuery(id+"F2.wireOp",EDGE,"E33.2.4.0"),sQuery(id+"F2.wireOp",EDGE,"E33.3.4.0"),sQuery(id+"F2.wireOp",EDGE,"E33.6.4.0"),sQuery(id+"F2.wireOp",EDGE,"E33.9.4.0"),sQuery(id+"F2.wireOp",EDGE,"E33.2.5.0"),sQuery(id+"F2.wireOp",EDGE,"E33.3.5.0"),sQuery(id+"F2.wireOp",EDGE,"E33.6.5.0"),sQuery(id+"F2.wireOp",EDGE,"E33.9.5.0"),sQuery(id+"F2.wireOp",EDGE,"E33.2.6.0"),sQuery(id+"F2.wireOp",EDGE,"E33.3.6.0"),sQuery(id+"F2.wireOp",EDGE,"E33.6.6.0"),sQuery(id+"F2.wireOp",EDGE,"E33.9.6.0"),sQuery(id+"F2.wireOp",EDGE,"E33.2.7.0"),sQuery(id+"F2.wireOp",EDGE,"E33.3.7.0"),sQuery(id+"F2.wireOp",EDGE,"E33.6.7.0"),sQuery(id+"F2.wireOp",EDGE,"E33.9.7.0"),sQuery(id+"F2.wireOp",EDGE,"E33.2.8.0"),sQuery(id+"F2.wireOp",EDGE,"E33.3.8.0"),sQuery(id+"F2.wireOp",EDGE,"E33.6.8.0"),sQuery(id+"F2.wireOp",EDGE,"E33.9.8.0"),sQuery(id+"F2.wireOp",EDGE,"E33.2.9.0"),sQuery(id+"F2.wireOp",EDGE,"E33.3.9.0"),sQuery(id+"F2.wireOp",EDGE,"E33.6.9.0"),sQuery(id+"F2.wireOp",EDGE,"E33.9.9.0"),sQuery(id+"F2.wireOp",EDGE,"E33.2.10.0"),sQuery(id+"F2.wireOp",EDGE,"E33.3.10.0"),sQuery(id+"F2.wireOp",EDGE,"E33.6.10.0"),sQuery(id+"F2.wireOp",EDGE,"E33.9.10.0"),sQuery(id+"F2.wireOp",EDGE,"E33.2.11.0"),sQuery(id+"F2.wireOp",EDGE,"E33.3.11.0"),sQuery(id+"F2.wireOp",EDGE,"E33.6.11.0"),sQuery(id+"F2.wireOp",EDGE,"E33.9.11.0"),sQuery(id+"F2.wireOp",EDGE,"E33.2.12.0"),sQuery(id+"F2.wireOp",EDGE,"E33.3.12.0"),sQuery(id+"F2.wireOp",EDGE,"E33.6.12.0"),sQuery(id+"F2.wireOp",EDGE,"E33.9.12.0"),sQuery(id+"F2.wireOp",EDGE,"E33.2.13.0"),sQuery(id+"F2.wireOp",EDGE,"E33.3.13.0"),sQuery(id+"F2.wireOp",EDGE,"E33.6.13.0"),sQuery(id+"F2.wireOp",EDGE,"E33.9.13.0"),sQuery(id+"F2.wireOp",EDGE,"E33.2.14.0"),sQuery(id+"F2.wireOp",EDGE,"E33.3.14.0"),sQuery(id+"F2.wireOp",EDGE,"E33.6.14.0"),sQuery(id+"F2.wireOp",EDGE,"E33.9.14.0"),sQuery(id+"F2.wireOp",EDGE,"E33.2.15.0"),sQuery(id+"F2.wireOp",EDGE,"E33.3.15.0"),sQuery(id+"F2.wireOp",EDGE,"E33.6.15.0"),sQuery(id+"F2.wireOp",EDGE,"E33.9.15.0"),sQuery(id+"F2.wireOp",EDGE,"E33.2.16.0"),sQuery(id+"F2.wireOp",EDGE,"E33.3.16.0"),sQuery(id+"F2.wireOp",EDGE,"E33.6.16.0"),sQuery(id+"F2.wireOp",EDGE,"E33.9.16.0"),sQuery(id+"F2.wireOp",EDGE,"E33.2.17.0"),sQuery(id+"F2.wireOp",EDGE,"E33.3.17.0"),sQuery(id+"F2.wireOp",EDGE,"E33.6.17.0"),sQuery(id+"F2.wireOp",EDGE,"E33.9.17.0"),sQuery(id+"F2.wireOp",EDGE,"E33.2.18.0"),sQuery(id+"F2.wireOp",EDGE,"E33.3.18.0"),sQuery(id+"F2.wireOp",EDGE,"E33.6.18.0"),sQuery(id+"F2.wireOp",EDGE,"E33.9.18.0"),sQuery(id+"F2.wireOp",EDGE,"E33.2.19.0"),sQuery(id+"F2.wireOp",EDGE,"E33.3.19.0"),sQuery(id+"F2.wireOp",EDGE,"E33.6.19.0"),sQuery(id+"F2.wireOp",EDGE,"E33.9.19.0"),sQuery(id+"F2.wireOp",EDGE,"E33.2.20.0"),sQuery(id+"F2.wireOp",EDGE,"E33.3.20.0"),sQuery(id+"F2.wireOp",EDGE,"E33.6.20.0"),sQuery(id+"F2.wireOp",EDGE,"E33.9.20.0"),sQuery(id+"F2.wireOp",EDGE,"E33.2.21.0"),sQuery(id+"F2.wireOp",EDGE,"E33.3.21.0"),sQuery(id+"F2.wireOp",EDGE,"E33.6.21.0"),sQuery(id+"F2.wireOp",EDGE,"E33.9.21.0"),sQuery(id+"F2.wireOp",EDGE,"E33.2.22.0"),sQuery(id+"F2.wireOp",EDGE,"E33.3.22.0"),sQuery(id+"F2.wireOp",EDGE,"E33.6.22.0"),sQuery(id+"F2.wireOp",EDGE,"E33.9.22.0"),sQuery(id+"F2.wireOp",EDGE,"E33.2.23.0"),sQuery(id+"F2.wireOp",EDGE,"E33.3.23.0"),sQuery(id+"F2.wireOp",EDGE,"E33.6.23.0"),sQuery(id+"F2.wireOp",EDGE,"E33.9.23.0"),sQuery(id+"F2.wireOp",EDGE,"E33.2.24.0"),sQuery(id+"F2.wireOp",EDGE,"E33.3.24.0"),sQuery(id+"F2.wireOp",EDGE,"E33.6.24.0"),sQuery(id+"F2.wireOp",EDGE,"E33.9.24.0"),sQuery(id+"F2.wireOp",EDGE,"E33.2.25.0"),sQuery(id+"F2.wireOp",EDGE,"E33.3.25.0"),sQuery(id+"F2.wireOp",EDGE,"E33.6.25.0"),sQuery(id+"F2.wireOp",EDGE,"E33.9.25.0"),sQuery(id+"F2.wireOp",EDGE,"E33.2.26.0"),sQuery(id+"F2.wireOp",EDGE,"E33.3.26.0"),sQuery(id+"F2.wireOp",EDGE,"E33.6.26.0"),sQuery(id+"F2.wireOp",EDGE,"E33.9.26.0"),sQuery(id+"F2.wireOp",EDGE,"E33.2.27.0"),sQuery(id+"F2.wireOp",EDGE,"E33.3.27.0"),sQuery(id+"F2.wireOp",EDGE,"E33.6.27.0"),sQuery(id+"F2.wireOp",EDGE,"E33.9.27.0"),sQuery(id+"F2.wireOp",EDGE,"E33.2.28.0"),sQuery(id+"F2.wireOp",EDGE,"E33.3.28.0"),sQuery(id+"F2.wireOp",EDGE,"E33.6.28.0"),sQuery(id+"F2.wireOp",EDGE,"E33.9.28.0"),sQuery(id+"F2.wireOp",EDGE,"E33.2.29.0"),sQuery(id+"F2.wireOp",EDGE,"E33.3.29.0"),sQuery(id+"F2.wireOp",EDGE,"E33.6.29.0"),sQuery(id+"F2.wireOp",EDGE,"E33.9.29.0")])]});
            var Q10;
            Q10=makeQuery(id+"F12.opExtrude","SWEPT_BODY",BODY,{"disambiguationData":[OSD([sQuery(id+"F11.wireOp",EDGE,"E45.bottom"),sQuery(id+"F11.wireOp",EDGE,"E45.top"),sQuery(id+"F11.wireOp",EDGE,"E45.left"),sQuery(id+"F11.wireOp",EDGE,"E45.right")])]});
            booleanBodies(context, id + "F13", {"operationType" : BooleanOperationType.SUBTRACTION, "tools" : qUnion([Q0, Q1, Q2, Q3, Q4]), "targets" : qUnion([Q5, Q6, Q7, Q8, Q9, Q10]), "keepTools" : true});
        }
    });
